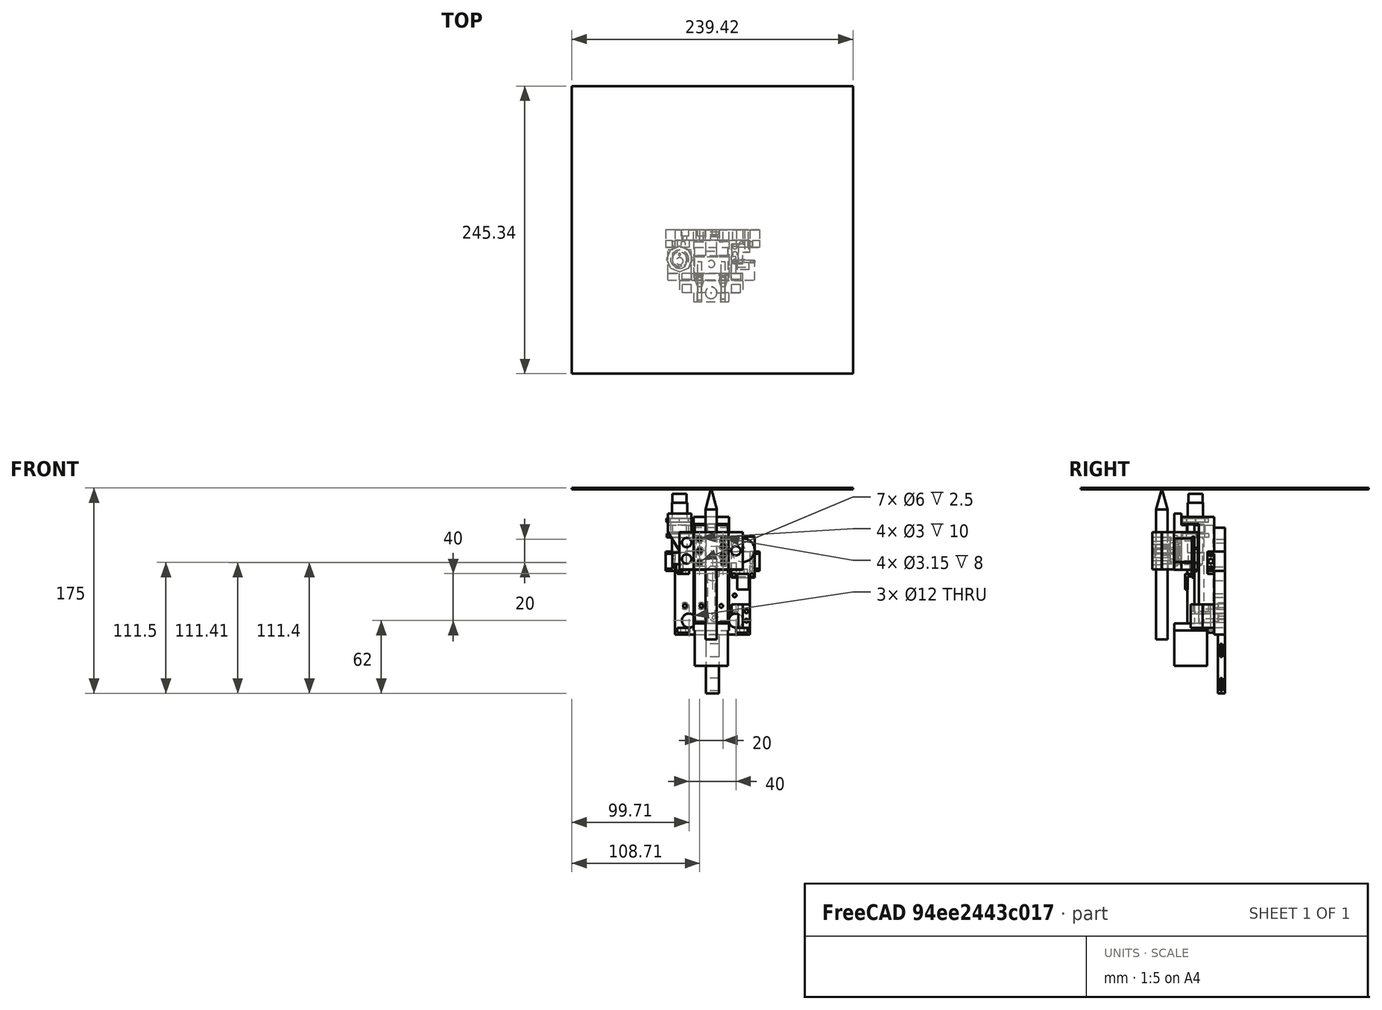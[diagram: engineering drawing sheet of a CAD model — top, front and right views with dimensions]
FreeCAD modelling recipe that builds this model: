
FCSTD DOCUMENT  (FreeCAD 1.0R39109 (Git))
Label: pen_plotter_head_v2a
License: All rights reserved
LicenseURL: https://en.wikipedia.org/wiki/All_rights_reserved
objects: Sketcher::SketchObject×76, PartDesign::Pad×47, PartDesign::Pocket×32, PartDesign::Body×13, PartDesign::Mirrored×5, PartDesign::LinearPattern×3, Mesh::Feature×2
note: 418 computed .brp shape members not serialized (recipe doc carries the construction recipe); baked Part::Feature solids carry a one-line shape summary decoded from their .brp

FEATURE [Mesh::Feature] Carriage_Plate_w_Threads
  Placement = pos=(32.05,21.1,32.2) rot=(0,0.707107,-0.707107;3.14159rad)
FEATURE [Mesh::Feature] _0x20_v_slot  label="20x20_v-slot"
  Placement = pos=(-48.6,20.5,0) rot=(0,0,-1;1.5708rad)
FEATURE [Sketcher::SketchObject] Sketch
  ArcFitTolerance = 1e-06
  AttachmentSupport = -> [XZ_Plane001]
  FullyConstrained = true
  MakeInternals = false
  MapMode = 5
  Placement = pos=(0,0,0) rot=(1,0,0;1.5708rad)
  sketch-geometry (5):
    g0: LineSegment StartX=-15 StartY=-48.5 StartZ=0 EndX=15 EndY=-48.5 EndZ=0
    g1: LineSegment StartX=15 StartY=-48.5 StartZ=0 EndX=15 EndY=48.5 EndZ=0
    g2: LineSegment StartX=15 StartY=48.5 StartZ=0 EndX=-15 EndY=48.5 EndZ=0
    g3: LineSegment StartX=-15 StartY=48.5 StartZ=0 EndX=-15 EndY=-48.5 EndZ=0
    g4: GeomPoint [constr] X=0 Y=0 Z=0
  constraints (12):
    c: Coincident(g0,g1)
    c: Coincident(g1,g2)
    c: Coincident(g2,g3)
    c: Coincident(g3,g0)
    c: Horizontal(g0)
    c: Horizontal(g2)
    c: Vertical(g1)
    c: Vertical(g3)
    c: Symmetric(g2,g0,g4)
    c: Distance(g1,g3) = 30
    c: Distance(g0,g2) = 97
    c: Coincident(g4,g-1)
FEATURE [PartDesign::Pad] Pad  label="Base"
  Direction = (0,-1,2e-16)
  Length = 13
  Length2 = 10
  Placement = pos=(0,0,0) rot=(1,0,0;1.5708rad)
  Profile = -> Sketch
  ReferenceAxis = -> Sketch [N_Axis]
  Refine = true
  Suppressed = false
  Type = 0
FEATURE [Sketcher::SketchObject] Sketch001
  ArcFitTolerance = 1e-06
  AttachmentSupport = -> [Pad]
  ExternalGeometry = -> [Pad]
  FullyConstrained = true
  MakeInternals = false
  MapMode = 5
  Placement = pos=(0,-13,0) rot=(1,0,0;1.5708rad)
  sketch-geometry (10):
    g0: LineSegment StartX=-15 StartY=-42.5 StartZ=0 EndX=-15 EndY=-48.5 EndZ=0
    g1: LineSegment StartX=-15 StartY=-48.5 StartZ=0 EndX=15 EndY=-48.5 EndZ=0
    g2: LineSegment StartX=15 StartY=-48.5 StartZ=0 EndX=15 EndY=-42.5 EndZ=0
    g3: LineSegment StartX=15 StartY=-42.5 StartZ=0 EndX=-15 EndY=-42.5 EndZ=0
    g4: GeomPoint [constr] X=0 Y=-45.5 Z=0
    g5: LineSegment StartX=-15 StartY=42.5 StartZ=0 EndX=15 EndY=42.5 EndZ=0
    g6: LineSegment StartX=15 StartY=42.5 StartZ=0 EndX=15 EndY=48.5 EndZ=0
    g7: LineSegment StartX=15 StartY=48.5 StartZ=0 EndX=-15 EndY=48.5 EndZ=0
    g8: LineSegment StartX=-15 StartY=48.5 StartZ=0 EndX=-15 EndY=42.5 EndZ=0
    g9: GeomPoint [constr] X=0 Y=45.5 Z=0
  constraints (24):
    c: Coincident(g0,g1)
    c: Coincident(g1,g2)
    c: Coincident(g2,g3)
    c: Coincident(g3,g0)
    c: Vertical(g0)
    c: Vertical(g2)
    c: Horizontal(g1)
    c: Horizontal(g3)
    c: Symmetric(g2,g0,g4)
    c: PointOnObject(g4,g-2)
    c: Coincident(g1,g-3)
    c: DistanceY(g1,g2) = 6
    c: Coincident(g5,g6)
    c: Coincident(g6,g7)
    c: Coincident(g7,g8)
    c: Coincident(g8,g5)
    c: Horizontal(g5)
    c: Horizontal(g7)
    c: Vertical(g6)
    c: Vertical(g8)
    c: Symmetric(g7,g5,g9)
    c: PointOnObject(g9,g-2)
    c: Coincident(g6,g-5)
    c: Equal(g6,g2)
FEATURE [PartDesign::Pad] Pad001  label="Flanges"
  BaseFeature = -> Pad
  Direction = (0,-1,2e-16)
  Length = 15
  Length2 = 10
  Placement = pos=(0,0,0) rot=(1,0,0;1.5708rad)
  Profile = -> Sketch001
  ReferenceAxis = -> Sketch001 [N_Axis]
  Refine = true
  Suppressed = false
  Type = 0
FEATURE [PartDesign::Pad] Pad002  label="FlangeExtension"
  BaseFeature = -> Pad001
  Direction = (0,-1,0)
  Length = 6
  Length2 = 10
  Placement = pos=(0,0,0) rot=(1,0,0;1.5708rad)
  Profile = -> Pad001 [Face5]
  Refine = true
  Suppressed = false
  Type = 0
FEATURE [Sketcher::SketchObject] Sketch002
  ArcFitTolerance = 1e-06
  AttachmentSupport = -> [Pad002]
  ExternalGeometry = -> [Pad002]
  FullyConstrained = true
  MakeInternals = false
  MapMode = 5
  Placement = pos=(0,2.09e-14,48.5) rot=(0,0,1;3.14159rad)
  sketch-geometry (5):
    g0: LineSegment StartX=-14 StartY=6 StartZ=0 EndX=14 EndY=6 EndZ=0
    g1: LineSegment StartX=14 StartY=6 StartZ=0 EndX=14 EndY=34 EndZ=0
    g2: LineSegment StartX=14 StartY=34 StartZ=0 EndX=-14 EndY=34 EndZ=0
    g3: LineSegment StartX=-14 StartY=34 StartZ=0 EndX=-14 EndY=6 EndZ=0
    g4: GeomPoint [constr] X=0 Y=20 Z=0
  constraints (13):
    c: Coincident(g0,g1)
    c: Coincident(g1,g2)
    c: Coincident(g2,g3)
    c: Coincident(g3,g0)
    c: Horizontal(g0)
    c: Horizontal(g2)
    c: Vertical(g1)
    c: Vertical(g3)
    c: Symmetric(g2,g0,g4)
    c: Distance(g1,g3) = 28
    c: PointOnObject(g2,g-3)
    c: PointOnObject(g4,g-2)
    c: Equal(g1,g2)
FEATURE [PartDesign::Pad] Pad003  label="Stepper"
  BaseFeature = -> Pad002
  Direction = (0,0,1)
  Length = 30
  Length2 = 10
  Placement = pos=(0,0,0) rot=(1,0,0;1.5708rad)
  Profile = -> Sketch002
  ReferenceAxis = -> Sketch002 [N_Axis]
  Refine = true
  Suppressed = false
  Type = 0
FEATURE [Sketcher::SketchObject] Sketch003
  ArcFitTolerance = 1e-06
  AttachmentSupport = -> [Pad003]
  FullyConstrained = false
  MakeInternals = false
  MapMode = 5
  Placement = pos=(0,-13,0) rot=(1,0,0;1.5708rad)
  sketch-geometry (5):
    g0: LineSegment StartX=-13 StartY=-32.4103 StartZ=0 EndX=13 EndY=-32.4103 EndZ=0
    g1: LineSegment StartX=13 StartY=-32.4103 StartZ=0 EndX=13 EndY=-6.41029 EndZ=0
    g2: LineSegment StartX=13 StartY=-6.41029 StartZ=0 EndX=-13 EndY=-6.41029 EndZ=0
    g3: LineSegment StartX=-13 StartY=-6.41029 StartZ=0 EndX=-13 EndY=-32.4103 EndZ=0
    g4: GeomPoint [constr] X=0 Y=-19.4103 Z=0
  constraints (12):
    c: Coincident(g0,g1)
    c: Coincident(g1,g2)
    c: Coincident(g2,g3)
    c: Coincident(g3,g0)
    c: Horizontal(g0)
    c: Horizontal(g2)
    c: Vertical(g1)
    c: Vertical(g3)
    c: Symmetric(g2,g0,g4)
    c: Distance(g1,g3) = 26
    c: Distance(g0,g2) = 26
    c: DistanceX(g-1,g4) = 0
FEATURE [PartDesign::Pad] Pad004  label="TableBase"
  BaseFeature = -> Pad003
  Direction = (0,-1,2e-16)
  Length = 1
  Length2 = 10
  Placement = pos=(0,0,0) rot=(1,0,0;1.5708rad)
  Profile = -> Sketch003
  ReferenceAxis = -> Sketch003 [N_Axis]
  Refine = true
  Suppressed = false
  Type = 0
FEATURE [Sketcher::SketchObject] Sketch004
  ArcFitTolerance = 1e-06
  AttachmentSupport = -> [Pad004]
  ExternalGeometry = -> [Pad004]
  FullyConstrained = true
  MakeInternals = false
  MapMode = 5
  Placement = pos=(0,-14,0) rot=(1,0,0;1.5708rad)
  sketch-geometry (8):
    g0: LineSegment StartX=-15 StartY=-35.4103 StartZ=0 EndX=15 EndY=-35.4103 EndZ=0
    g1: LineSegment StartX=15 StartY=-35.4103 StartZ=0 EndX=15 EndY=-3.41029 EndZ=0
    g2: LineSegment StartX=15 StartY=-3.41029 StartZ=0 EndX=-15 EndY=-3.41029 EndZ=0
    g3: LineSegment StartX=-15 StartY=-3.41029 StartZ=0 EndX=-15 EndY=-35.4103 EndZ=0
    g4: GeomPoint [constr] X=0 Y=-19.4103 Z=0
    g5: GeomPoint [constr] X=13 Y=-19.4103 Z=0
    g6: GeomPoint [constr] X=-3e-16 Y=-6.41029 Z=0
    g7: GeomPoint [constr] X=0 Y=-19.4103 Z=0
  constraints (16):
    c: Coincident(g0,g1)
    c: Coincident(g1,g2)
    c: Coincident(g2,g3)
    c: Coincident(g3,g0)
    c: Horizontal(g0)
    c: Horizontal(g2)
    c: Vertical(g1)
    c: Vertical(g3)
    c: Symmetric(g2,g0,g4)
    c: Distance(g1,g3) = 30
    c: Distance(g0,g2) = 32
    c: DistanceX(g-1,g4) = 0
    c: Symmetric(g-4,g-4,g5)
    c: Symmetric(g-3,g-3,g6)
    c: DistanceY(g5,g7) = 0
    c: Coincident(g4,g7)
FEATURE [PartDesign::Pad] Pad005  label="TableMount"
  BaseFeature = -> Pad004
  Direction = (0,-1,2e-16)
  Length = 14
  Length2 = 10
  Placement = pos=(0,0,0) rot=(1,0,0;1.5708rad)
  Profile = -> Sketch004
  ReferenceAxis = -> Sketch004 [N_Axis]
  Refine = true
  Suppressed = false
  Type = 0
FEATURE [Sketcher::SketchObject] Sketch005
  ArcFitTolerance = 1e-06
  AttachmentSupport = -> [Pad005]
  ExternalGeometry = -> [Pad005]
  FullyConstrained = true
  MakeInternals = false
  MapMode = 5
  Placement = pos=(0,-28,6.2e-15) rot=(1,0,0;1.5708rad)
  sketch-geometry (4):
    g0: Circle CenterX=-10 CenterY=-9.41029 CenterZ=0 NormalX=0 NormalY=0 NormalZ=1 AngleXU=0 Radius=1.5
    g1: Circle CenterX=10 CenterY=-9.41029 CenterZ=0 NormalX=0 NormalY=0 NormalZ=1 AngleXU=0 Radius=1.5
    g2: Circle CenterX=10 CenterY=-29.4103 CenterZ=0 NormalX=0 NormalY=0 NormalZ=1 AngleXU=0 Radius=1.5
    g3: Circle CenterX=-10 CenterY=-29.4103 CenterZ=0 NormalX=0 NormalY=0 NormalZ=1 AngleXU=0 Radius=1.5
  constraints (12):
    c: Diameter(g0) = 3
    c: Equal(g1,g0)
    c: Equal(g0,g3)
    c: Equal(g3,g2)
    c: DistanceY(g0,g-5) = 6
    c: DistanceX(g-5,g0) = 5
    c: DistanceY(g1,g0) = 0
    c: DistanceX(g3,g0) = 0
    c: DistanceY(g3,g2) = 0
    c: DistanceX(g2,g1) = 0
    c: DistanceY(g3,g0) = 20
    c: DistanceX(g0,g1) = 20
FEATURE [PartDesign::Pocket] Pocket  label="TableMountingHoles"
  BaseFeature = -> Pad005
  Direction = (0,1,-2e-16)
  Length = 10
  Length2 = 5
  Placement = pos=(0,0,0) rot=(1,0,0;1.5708rad)
  Profile = -> Sketch005
  ReferenceAxis = -> Sketch005 [N_Axis]
  Refine = true
  Suppressed = false
  Type = 0
FEATURE [Sketcher::SketchObject] Sketch006
  ArcFitTolerance = 1e-06
  AttachmentSupport = -> [Pocket]
  ExternalGeometry = -> [Pocket]
  FullyConstrained = true
  MakeInternals = false
  MapMode = 5
  Placement = pos=(0,2.55e-14,42.5) rot=(1,0,0;3.14159rad)
  sketch-geometry (1):
    g0: Circle CenterX=0 CenterY=20 CenterZ=0 NormalX=0 NormalY=0 NormalZ=1 AngleXU=0 Radius=3
  constraints (3):
    c: PointOnObject(g0,g-2)
    c: DistanceY(g0,g-3) = 14
    c: Diameter(g0) = 6
FEATURE [PartDesign::Pad] Pad006  label="BallScrew"
  BaseFeature = -> Pocket
  Direction = (0,0,-1)
  Length = 85
  Length2 = 10
  Placement = pos=(0,0,0) rot=(1,0,0;1.5708rad)
  Profile = -> Sketch006
  ReferenceAxis = -> Sketch006 [N_Axis]
  Refine = true
  Suppressed = false
  Type = 0
FEATURE [Sketcher::SketchObject] Sketch007
  ArcFitTolerance = 1e-06
  AttachmentSupport = -> [Pad006]
  FullyConstrained = true
  MakeInternals = false
  MapMode = 5
  Placement = pos=(0,-13,0) rot=(1,0,0;1.5708rad)
  sketch-geometry (5):
    g0: LineSegment StartX=-4.5 StartY=-42.5 StartZ=0 EndX=4.5 EndY=-42.5 EndZ=0
    g1: LineSegment StartX=4.5 StartY=-42.5 StartZ=0 EndX=4.5 EndY=42.5 EndZ=0
    g2: LineSegment StartX=4.5 StartY=42.5 StartZ=0 EndX=-4.5 EndY=42.5 EndZ=0
    g3: LineSegment StartX=-4.5 StartY=42.5 StartZ=0 EndX=-4.5 EndY=-42.5 EndZ=0
    g4: GeomPoint [constr] X=0 Y=0 Z=0
  constraints (12):
    c: Coincident(g0,g1)
    c: Coincident(g1,g2)
    c: Coincident(g2,g3)
    c: Coincident(g3,g0)
    c: Horizontal(g0)
    c: Horizontal(g2)
    c: Vertical(g1)
    c: Vertical(g3)
    c: Symmetric(g2,g0,g4)
    c: Distance(g1,g3) = 9
    c: Distance(g0,g2) = 85
    c: Coincident(g4,g-1)
FEATURE [Sketcher::SketchObject] Sketch009
  ArcFitTolerance = 1e-06
  AttachmentSupport = -> [XZ_Plane002]
  FullyConstrained = true
  MakeInternals = false
  MapMode = 5
  Placement = pos=(0,0,0) rot=(1,0,0;1.5708rad)
  sketch-geometry (7):
    g0: LineSegment StartX=-10 StartY=-17.5 StartZ=0 EndX=10 EndY=-17.5 EndZ=0
    g1: LineSegment StartX=10 StartY=-17.5 StartZ=0 EndX=10 EndY=17.5 EndZ=0
    g2: LineSegment StartX=10 StartY=17.5 StartZ=0 EndX=-10 EndY=17.5 EndZ=0
    g3: LineSegment StartX=-10 StartY=17.5 StartZ=0 EndX=-10 EndY=-17.5 EndZ=0
    g4: GeomPoint [constr] X=0 Y=0 Z=0
    g5: Circle CenterX=7.7 CenterY=15.2 CenterZ=0 NormalX=0 NormalY=0 NormalZ=1 AngleXU=0 Radius=1.5
    g6: Circle CenterX=-7.7 CenterY=15.2 CenterZ=0 NormalX=0 NormalY=0 NormalZ=1 AngleXU=0 Radius=1.5
  constraints (17):
    c: Coincident(g0,g1)
    c: Coincident(g1,g2)
    c: Coincident(g2,g3)
    c: Coincident(g3,g0)
    c: Horizontal(g0)
    c: Horizontal(g2)
    c: Vertical(g1)
    c: Vertical(g3)
    c: Symmetric(g2,g0,g4)
    c: Distance(g1,g3) = 20
    c: Distance(g0,g2) = 35
    c: Coincident(g4,g-1)
    c: Diameter(g5) = 3
    c: Equal(g5,g6)
    c: DistanceX(g5,g1) = 2.3
    c: DistanceY(g5,g1) = 2.3
    c: Symmetric(g6,g5,g-2)
FEATURE [PartDesign::Pad] Pad007  label="Base002"
  Direction = (0,-1,2e-16)
  Length = 2
  Length2 = 10
  Placement = pos=(0,0,0) rot=(1,0,0;1.5708rad)
  Profile = -> Sketch009
  ReferenceAxis = -> Sketch009 [N_Axis]
  Refine = true
  Suppressed = false
  Type = 0
FEATURE [Sketcher::SketchObject] Sketch010
  ArcFitTolerance = 1e-06
  AttachmentSupport = -> [Pad007]
  FullyConstrained = true
  MakeInternals = false
  MapMode = 5
  Placement = pos=(0,-2,0) rot=(1,0,0;1.5708rad)
  sketch-geometry (1):
    g0: Circle CenterX=0 CenterY=-6 CenterZ=0 NormalX=0 NormalY=0 NormalZ=1 AngleXU=0 Radius=10
  constraints (3):
    c: Diameter(g0) = 20
    c: PointOnObject(g0,g-2)
    c: DistanceY(g-3,g0) = 14
FEATURE [PartDesign::Pad] Pad008
  BaseFeature = -> Pad007
  Direction = (0,-1,2e-16)
  Length = 15
  Length2 = 10
  Placement = pos=(0,0,0) rot=(1,0,0;1.5708rad)
  Profile = -> Sketch010
  ReferenceAxis = -> Sketch010 [N_Axis]
  Refine = true
  Suppressed = false
  Type = 0
FEATURE [Sketcher::SketchObject] Sketch011
  ArcFitTolerance = 1e-06
  AttachmentSupport = -> [Pad008]
  ExternalGeometry = -> [Pad008]
  FullyConstrained = true
  MakeInternals = false
  MapMode = 5
  Placement = pos=(0,4e-16,0) rot=(-1,0,0;1.5708rad)
  sketch-geometry (1):
    g0: Circle CenterX=0 CenterY=7.5 CenterZ=0 NormalX=0 NormalY=0 NormalZ=1 AngleXU=0 Radius=1.5
  constraints (3):
    c: Diameter(g0) = 3
    c: PointOnObject(g0,g-2)
    c: DistanceY(g0,g-3) = 10
FEATURE [PartDesign::Pad] Pad009
  BaseFeature = -> Pad008
  Direction = (0,1,2e-16)
  Length = 1
  Length2 = 10
  Placement = pos=(0,0,0) rot=(1,0,0;1.5708rad)
  Profile = -> Sketch011
  ReferenceAxis = -> Sketch011 [N_Axis]
  Refine = true
  Suppressed = false
  Type = 0
FEATURE [Sketcher::SketchObject] Sketch012
  ArcFitTolerance = 1e-06
  AttachmentSupport = -> [Pad009]
  ExternalGeometry = -> [Pad009]
  FullyConstrained = true
  MakeInternals = false
  MapMode = 5
  Placement = pos=(0,-2,0) rot=(1,0,0;1.5708rad)
  sketch-geometry (5):
    g0: LineSegment StartX=-5 StartY=14.2 StartZ=0 EndX=5 EndY=14.2 EndZ=0
    g1: LineSegment StartX=5 StartY=14.2 StartZ=0 EndX=5 EndY=16.5 EndZ=0
    g2: LineSegment StartX=5 StartY=16.5 StartZ=0 EndX=-5 EndY=16.5 EndZ=0
    g3: LineSegment StartX=-5 StartY=16.5 StartZ=0 EndX=-5 EndY=14.2 EndZ=0
    g4: GeomPoint [constr] X=0 Y=15.35 Z=0
  constraints (13):
    c: Coincident(g0,g1)
    c: Coincident(g1,g2)
    c: Coincident(g2,g3)
    c: Coincident(g3,g0)
    c: Horizontal(g0)
    c: Horizontal(g2)
    c: Vertical(g1)
    c: Vertical(g3)
    c: Symmetric(g2,g0,g4)
    c: Distance(g1,g3) = 10
    c: Distance(g0,g2) = 2.3
    c: PointOnObject(g4,g-2)
    c: DistanceY(g4,g-3) = 2.15
FEATURE [PartDesign::Pad] Pad010
  BaseFeature = -> Pad009
  Direction = (0,-1,2e-16)
  Length = 6
  Length2 = 10
  Placement = pos=(0,0,0) rot=(1,0,0;1.5708rad)
  Profile = -> Sketch012
  ReferenceAxis = -> Sketch012 [N_Axis]
  Refine = true
  Suppressed = false
  Type = 0
FEATURE [Sketcher::SketchObject] Sketch013
  ArcFitTolerance = 1e-06
  AttachmentSupport = -> [Pad010]
  ExternalGeometry = -> [Pad010]
  FullyConstrained = true
  MakeInternals = false
  MapMode = 5
  Placement = pos=(0,7.3e-15,16.5) rot=(0,0,1;3.14159rad)
  sketch-geometry (5):
    g0: LineSegment StartX=5 StartY=5.7 StartZ=0 EndX=5 EndY=8 EndZ=0
    g1: LineSegment StartX=5 StartY=8 StartZ=0 EndX=-5 EndY=8 EndZ=0
    g2: LineSegment StartX=-5 StartY=8 StartZ=0 EndX=-5 EndY=5.7 EndZ=0
    g3: LineSegment StartX=-5 StartY=5.7 StartZ=0 EndX=5 EndY=5.7 EndZ=0
    g4: GeomPoint [constr] X=0 Y=6.85 Z=0
  constraints (12):
    c: Coincident(g0,g1)
    c: Coincident(g1,g2)
    c: Coincident(g2,g3)
    c: Coincident(g3,g0)
    c: Vertical(g0)
    c: Vertical(g2)
    c: Horizontal(g1)
    c: Horizontal(g3)
    c: Symmetric(g2,g0,g4)
    c: PointOnObject(g4,g-2)
    c: DistanceY(g0,g0) = 2.3
    c: Coincident(g0,g-3)
FEATURE [PartDesign::Pad] Pad011
  BaseFeature = -> Pad010
  Direction = (0,0,1)
  Length = 11
  Length2 = 10
  Placement = pos=(0,0,0) rot=(1,0,0;1.5708rad)
  Profile = -> Sketch013
  ReferenceAxis = -> Sketch013 [N_Axis]
  Refine = true
  Suppressed = false
  Type = 0
FEATURE [PartDesign::Body] Body002  label="ElectroMagnetKeyStudio25N5V"
  AllowCompound = false
  Group = -> [Sketch009,Pad007,Sketch010,Pad008,Sketch011,Pad009,Sketch012,Pad010,Sketch013,Pad011]
  Origin = -> Origin002
  Placement = pos=(26,-26,34) rot=(0,1,0;3.14159rad)
  Tip = -> Pad011
FEATURE [Sketcher::SketchObject] Sketch014
  ArcFitTolerance = 1e-06
  AttachmentSupport = -> [XY_Plane003]
  FullyConstrained = true
  MakeInternals = false
  MapMode = 5
  sketch-geometry (1):
    g0: Circle CenterX=0 CenterY=0 CenterZ=0 NormalX=0 NormalY=0 NormalZ=1 AngleXU=0 Radius=6
  constraints (2):
    c: Diameter(g0) = 12
    c: Coincident(g0,g-1)
FEATURE [PartDesign::Pad] Pad012  label="SensorHead"
  Direction = (0,0,1)
  Length = 7.5
  Length2 = 10
  Profile = -> Sketch014
  ReferenceAxis = -> Sketch014 [N_Axis]
  Refine = true
  Suppressed = false
  Type = 0
FEATURE [Sketcher::SketchObject] Sketch015
  ArcFitTolerance = 1e-06
  AttachmentSupport = -> [Pad012]
  FullyConstrained = true
  MakeInternals = false
  MapMode = 5
  Placement = pos=(0,0,7.5) rot=(0,0,1;0rad)
  sketch-geometry (1):
    g0: Circle CenterX=0 CenterY=0 CenterZ=0 NormalX=0 NormalY=0 NormalZ=1 AngleXU=0 Radius=6.5
  constraints (2):
    c: Diameter(g0) = 13
    c: Coincident(g0,g-1)
FEATURE [PartDesign::Pad] Pad013  label="SensorThread"
  BaseFeature = -> Pad012
  Direction = (0,0,1)
  Length = 42.5
  Length2 = 10
  Profile = -> Sketch015
  ReferenceAxis = -> Sketch015 [N_Axis]
  Refine = true
  Suppressed = false
  Type = 0
FEATURE [Sketcher::SketchObject] Sketch016
  ArcFitTolerance = 1e-06
  AttachmentSupport = -> [Pad013]
  FullyConstrained = true
  MakeInternals = false
  MapMode = 5
  Placement = pos=(0,0,50) rot=(0,0,1;0rad)
  sketch-geometry (1):
    g0: Circle CenterX=0 CenterY=0 CenterZ=0 NormalX=0 NormalY=0 NormalZ=1 AngleXU=0 Radius=6
  constraints (2):
    c: Diameter(g0) = 12
    c: Coincident(g0,g-1)
FEATURE [PartDesign::Pad] Pad014  label="SensorBody"
  BaseFeature = -> Pad013
  Direction = (0,0,1)
  Length = 10
  Length2 = 10
  Profile = -> Sketch016
  ReferenceAxis = -> Sketch016 [N_Axis]
  Refine = true
  Suppressed = false
  Type = 0
FEATURE [Sketcher::SketchObject] Sketch017
  ArcFitTolerance = 1e-06
  AttachmentSupport = -> [Pad014]
  FullyConstrained = false
  MakeInternals = false
  MapMode = 5
  Placement = pos=(0,0,60) rot=(0,0,1;0rad)
  sketch-geometry (1):
    g0: Circle CenterX=0 CenterY=-1.61854 CenterZ=0 NormalX=0 NormalY=0 NormalZ=1 AngleXU=0 Radius=3
  constraints (2):
    c: Diameter(g0) = 6
    c: PointOnObject(g0,g-2)
FEATURE [PartDesign::Pad] Pad015  label="SensorCable"
  BaseFeature = -> Pad014
  Direction = (0,0,1)
  Length = 6
  Length2 = 10
  Profile = -> Sketch017
  ReferenceAxis = -> Sketch017 [N_Axis]
  Refine = true
  Suppressed = false
  Type = 0
FEATURE [Sketcher::SketchObject] Sketch018
  ArcFitTolerance = 1e-06
  AttachmentSupport = -> [Pad015]
  FullyConstrained = false
  MakeInternals = false
  MapMode = 5
  Placement = pos=(0,0,60) rot=(0,0,1;0rad)
  sketch-geometry (1):
    g0: Circle CenterX=0 CenterY=4.04203 CenterZ=0 NormalX=0 NormalY=0 NormalZ=1 AngleXU=0 Radius=1
FEATURE [PartDesign::Pad] Pad016  label="SensorLED"
  BaseFeature = -> Pad015
  Direction = (0,0,1)
  Length = 1
  Length2 = 10
  Profile = -> Sketch018
  ReferenceAxis = -> Sketch018 [N_Axis]
  Refine = true
  Suppressed = false
  Type = 0
FEATURE [Sketcher::SketchObject] Sketch019
  ArcFitTolerance = 1e-06
  AttachmentOffset = pos=(0,0,-24) rot=(0,0,1;0rad)
  AttachmentSupport = -> [Pad016]
  FullyConstrained = false
  MakeInternals = false
  MapMode = 5
  Placement = pos=(0,0,24) rot=(1,0,0;3.14159rad)
  sketch-geometry (9):
    g0: LineSegment StartX=0 StartY=10.7223 StartZ=0 EndX=-7.73863 EndY=7.4066 EndZ=0
    g1: LineSegment StartX=-7.73863 StartY=7.4066 StartZ=0 EndX=-10.8661 EndY=-0.409983 EndZ=0
    g2: LineSegment StartX=-10.8661 StartY=-0.409983 StartZ=0 EndX=-7.55045 EndY=-8.14861 EndZ=0
    g3: LineSegment StartX=-7.55045 StartY=-8.14861 StartZ=0 EndX=0.266132 EndY=-11.2761 EndZ=0
    g4: LineSegment StartX=0.266132 StartY=-11.2761 StartZ=0 EndX=8.00476 EndY=-7.96043 EndZ=0
    g5: LineSegment StartX=8.00476 StartY=-7.96043 StartZ=0 EndX=11.1323 EndY=-0.143851 EndZ=0
    g6: LineSegment StartX=11.1323 StartY=-0.143851 StartZ=0 EndX=7.81658 EndY=7.59478 EndZ=0
    g7: LineSegment StartX=7.81658 StartY=7.59478 StartZ=0 EndX=0 EndY=10.7223 EndZ=0
    g8: Circle [constr] CenterX=0.133066 CenterY=-0.276917 CenterZ=0 NormalX=0 NormalY=0 NormalZ=1 AngleXU=0 Radius=11
  constraints (19):
    c: Coincident(g0,g1)
    c: Coincident(g1,g2)
    c: Coincident(g2,g3)
    c: Coincident(g3,g4)
    c: Coincident(g4,g5)
    c: Coincident(g5,g6)
    c: Coincident(g6,g7)
    c: Coincident(g7,g0)
    c: Equal(g0, g1-g7) x7
    c: PointOnObject(g0,g8)
    c: PointOnObject(g1,g8)
    c: PointOnObject(g2,g8)
    c: PointOnObject(g3,g8)
    c: PointOnObject(g4,g8)
    c: PointOnObject(g5,g8)
    c: PointOnObject(g6,g8)
    c: PointOnObject(g7,g8)
    c: Radius(g8) = 11
    c: PointOnObject(g7,g-2)
FEATURE [PartDesign::Pad] Pad017  label="SensorNut"
  BaseFeature = -> Pad016
  Direction = (0,0,-1)
  Length = 3
  Length2 = 10
  Profile = -> Sketch019
  ReferenceAxis = -> Sketch019 [N_Axis]
  Refine = true
  Suppressed = false
  Type = 0
FEATURE [Sketcher::SketchObject] Sketch020
  ArcFitTolerance = 1e-06
  AttachmentSupport = -> [Pad017]
  FullyConstrained = false
  MakeInternals = false
  MapMode = 5
  Placement = pos=(0,0,24) rot=(0,0,1;0rad)
  sketch-geometry (1):
    g0: Circle CenterX=0 CenterY=0 CenterZ=0 NormalX=0 NormalY=0 NormalZ=1 AngleXU=0 Radius=7.74183
  constraints (1):
    c: Coincident(g0,g-1)
FEATURE [PartDesign::Pad] Pad018  label="SensorSpacer"
  BaseFeature = -> Pad017
  Direction = (0,0,1)
  Length = 10
  Length2 = 10
  Profile = -> Sketch020
  ReferenceAxis = -> Sketch020 [N_Axis]
  Refine = true
  Suppressed = false
  Type = 0
FEATURE [Sketcher::SketchObject] Sketch021
  ArcFitTolerance = 1e-06
  AttachmentSupport = -> [Pad018]
  FullyConstrained = true
  MakeInternals = false
  MapMode = 5
  Placement = pos=(0,0,34) rot=(0,0,1;0rad)
  sketch-geometry (9):
    g0: LineSegment StartX=0 StartY=11 StartZ=0 EndX=-7.77817 EndY=7.77817 EndZ=0
    g1: LineSegment StartX=-7.77817 StartY=7.77817 StartZ=0 EndX=-11 EndY=-1.61604e-11 EndZ=0
    g2: LineSegment StartX=-11 StartY=-1.61604e-11 StartZ=0 EndX=-7.77817 EndY=-7.77817 EndZ=0
    g3: LineSegment StartX=-7.77817 StartY=-7.77817 StartZ=0 EndX=3.23208e-11 EndY=-11 EndZ=0
    g4: LineSegment StartX=3.23208e-11 StartY=-11 StartZ=0 EndX=7.77817 EndY=-7.77817 EndZ=0
    g5: LineSegment StartX=7.77817 StartY=-7.77817 StartZ=0 EndX=11 EndY=4.84821e-11 EndZ=0
    g6: LineSegment StartX=11 StartY=4.84821e-11 StartZ=0 EndX=7.77817 EndY=7.77817 EndZ=0
    g7: LineSegment StartX=7.77817 StartY=7.77817 StartZ=0 EndX=0 EndY=11 EndZ=0
    g8: Circle [constr] CenterX=0 CenterY=0 CenterZ=0 NormalX=0 NormalY=0 NormalZ=1 AngleXU=0 Radius=11
  constraints (20):
    c: Coincident(g0,g1)
    c: Coincident(g1,g2)
    c: Coincident(g2,g3)
    c: Coincident(g3,g4)
    c: Coincident(g4,g5)
    c: Coincident(g5,g6)
    c: Coincident(g6,g7)
    c: Coincident(g7,g0)
    c: Equal(g0, g1-g7) x7
    c: PointOnObject(g0,g8)
    c: PointOnObject(g1,g8)
    c: PointOnObject(g2,g8)
    c: PointOnObject(g3,g8)
    c: PointOnObject(g4,g8)
    c: PointOnObject(g5,g8)
    c: PointOnObject(g6,g8)
    c: PointOnObject(g7,g8)
    c: Radius(g8) = 11
    c: Coincident(g8,g-1)
    c: PointOnObject(g7,g-2)
FEATURE [PartDesign::Pad] Pad019  label="SensorNut2"
  BaseFeature = -> Pad018
  Direction = (0,0,1)
  Length = 3
  Length2 = 10
  Profile = -> Sketch021
  ReferenceAxis = -> Sketch021 [N_Axis]
  Refine = true
  Suppressed = false
  Type = 0
FEATURE [PartDesign::Body] Body003  label="InductiveProximitySensorM12"
  AllowCompound = false
  Group = -> [Sketch014,Pad012,Sketch015,Pad013,Sketch016,Pad014,Sketch017,Pad015,Sketch018,Pad016,Sketch019,Pad017,Sketch020,Pad018,Sketch021,Pad019]
  Origin = -> Origin003
  Placement = pos=(-28,-25,88) rot=(0,1,0;3.14159rad)
  Tip = -> Pad019
FEATURE [Sketcher::SketchObject] Sketch022
  ArcFitTolerance = 1e-06
  AttachmentSupport = -> [XZ_Plane]
  FullyConstrained = true
  MakeInternals = false
  MapMode = 5
  Placement = pos=(0,0,0) rot=(1,0,0;1.5708rad)
  sketch-geometry (5):
    g0: LineSegment StartX=-32 StartY=-32 StartZ=0 EndX=32 EndY=-32 EndZ=0
    g1: LineSegment StartX=32 StartY=-32 StartZ=0 EndX=32 EndY=32 EndZ=0
    g2: LineSegment StartX=32 StartY=32 StartZ=0 EndX=-32 EndY=32 EndZ=0
    g3: LineSegment StartX=-32 StartY=32 StartZ=0 EndX=-32 EndY=-32 EndZ=0
    g4: GeomPoint [constr] X=0 Y=0 Z=0
  constraints (12):
    c: Coincident(g0,g1)
    c: Coincident(g1,g2)
    c: Coincident(g2,g3)
    c: Coincident(g3,g0)
    c: Horizontal(g0)
    c: Horizontal(g2)
    c: Vertical(g1)
    c: Vertical(g3)
    c: Symmetric(g2,g0,g4)
    c: Distance(g1,g3) = 64
    c: Distance(g0,g2) = 64
    c: Coincident(g4,g-1)
FEATURE [PartDesign::Pad] Pad020  label="BackingPlate"
  Direction = (0,-1,2e-16)
  Length = 9
  Length2 = 10
  Placement = pos=(0,0,0) rot=(1,0,0;1.5708rad)
  Profile = -> Sketch022
  ReferenceAxis = -> Sketch022 [N_Axis]
  Refine = true
  Suppressed = false
  Type = 0
FEATURE [Sketcher::SketchObject] Sketch023
  ArcFitTolerance = 1e-06
  AttachmentSupport = -> [Pad020]
  ExternalGeometry = -> [Pad020]
  FullyConstrained = true
  MakeInternals = false
  MapMode = 5
  Placement = pos=(0,0,0) rot=(-1,0,0;1.5708rad)
  sketch-geometry (2):
    g0: Circle CenterX=-9.5 CenterY=7.5 CenterZ=0 NormalX=0 NormalY=0 NormalZ=1 AngleXU=0 Radius=1.55
    g1: Circle CenterX=-23.5 CenterY=7.5 CenterZ=0 NormalX=0 NormalY=0 NormalZ=1 AngleXU=0 Radius=1.55
  constraints (6):
    c: Diameter(g0) = 3.1
    c: Equal(g1,g0)
    c: DistanceY(g1,g0) = 0
    c: DistanceY(g1,g-3) = 24.5
    c: DistanceX(g-4,g1) = 8.5
    c: DistanceX(g1,g0) = 14
FEATURE [PartDesign::Pocket] Pocket003  label="CaptiveNutScrewHole"
  BaseFeature = -> Pad020
  Direction = (0,-1,-2e-16)
  Length = 9
  Length2 = 5
  Placement = pos=(0,0,0) rot=(1,0,0;1.5708rad)
  Profile = -> Sketch023
  ReferenceAxis = -> Sketch023 [N_Axis]
  Refine = true
  Suppressed = false
  Type = 0
FEATURE [Sketcher::SketchObject] Sketch024
  ArcFitTolerance = 1e-06
  AttachmentSupport = -> [Pocket003]
  ExternalGeometry = -> [Pocket003]
  FullyConstrained = true
  MakeInternals = false
  MapMode = 5
  Placement = pos=(0,0,0) rot=(-1,0,0;1.5708rad)
  sketch-geometry (2):
    g0: Circle CenterX=1.4 CenterY=17.5 CenterZ=0 NormalX=0 NormalY=0 NormalZ=1 AngleXU=0 Radius=1.55
    g1: Circle CenterX=18.9 CenterY=-1.5 CenterZ=0 NormalX=0 NormalY=0 NormalZ=1 AngleXU=0 Radius=1.55
  constraints (6):
    c: Diameter(g0) = 3.1
    c: Diameter(g1) = 3.1
    c: DistanceY(g0,g-4) = 14.5
    c: DistanceY(g1,g0) = 19
    c: DistanceX(g1,g-4) = 13.1
    c: DistanceX(g0,g1) = 17.5
FEATURE [PartDesign::Pocket] Pocket004  label="ThreadedHoleScrewHole"
  BaseFeature = -> Pocket003
  Direction = (0,-1,-2e-16)
  Length = 9
  Length2 = 5
  Placement = pos=(0,0,0) rot=(1,0,0;1.5708rad)
  Profile = -> Sketch024
  ReferenceAxis = -> Sketch024 [N_Axis]
  Refine = true
  Suppressed = false
  Type = 0
FEATURE [Sketcher::SketchObject] Sketch025
  ArcFitTolerance = 1e-06
  AttachmentSupport = -> [Pocket004]
  ExternalGeometry = -> [Pocket004]
  FullyConstrained = true
  MakeInternals = false
  MapMode = 5
  Placement = pos=(0,0,0) rot=(-1,0,0;1.5708rad)
  sketch-geometry (2):
    g0: Circle CenterX=-23.5 CenterY=7.5 CenterZ=0 NormalX=0 NormalY=0 NormalZ=1 AngleXU=0 Radius=3
    g1: Circle CenterX=-9.5 CenterY=7.5 CenterZ=0 NormalX=0 NormalY=0 NormalZ=1 AngleXU=0 Radius=3
  constraints (4):
    c: Diameter(g0) = 6
    c: Coincident(g0,g-3)
    c: Diameter(g1) = 6
    c: Coincident(g1,g-4)
FEATURE [PartDesign::Pocket] Pocket005  label="CaptiveNutHole"
  BaseFeature = -> Pocket004
  Direction = (0,-1,-2e-16)
  Length = 5.5
  Length2 = 5
  Placement = pos=(0,0,0) rot=(1,0,0;1.5708rad)
  Profile = -> Sketch025
  ReferenceAxis = -> Sketch025 [N_Axis]
  Refine = true
  Suppressed = false
  Type = 0
FEATURE [Sketcher::SketchObject] Sketch026
  ArcFitTolerance = 1e-06
  AttachmentSupport = -> [Pocket005]
  ExternalGeometry = -> [Pocket005]
  FullyConstrained = true
  MakeInternals = false
  MapMode = 5
  Placement = pos=(0,0,0) rot=(-1,0,0;1.5708rad)
  sketch-geometry (3):
    g0: Circle CenterX=0 CenterY=-20 CenterZ=0 NormalX=0 NormalY=0 NormalZ=1 AngleXU=0 Radius=6
    g1: Circle CenterX=20 CenterY=20 CenterZ=0 NormalX=0 NormalY=0 NormalZ=1 AngleXU=0 Radius=6
    g2: Circle CenterX=-20 CenterY=20 CenterZ=0 NormalX=0 NormalY=0 NormalZ=1 AngleXU=0 Radius=6
  constraints (9):
    c: Diameter(g0) = 12
    c: PointOnObject(g0,g-2)
    c: Equal(g0,g1)
    c: DistanceX(g1,g-3) = 12
    c: DistanceX(g2,g1) = 40
    c: DistanceY(g1,g2) = 0
    c: DistanceY(g1,g-3) = 12
    c: DistanceY(g0,g-3) = 52
    c: Equal(g2,g1)
FEATURE [PartDesign::Pocket] Pocket006  label="WheelNutCutouts"
  BaseFeature = -> Pocket005
  Direction = (0,-1,-2e-16)
  Length = 9
  Length2 = 5
  Placement = pos=(0,0,0) rot=(1,0,0;1.5708rad)
  Profile = -> Sketch026
  ReferenceAxis = -> Sketch026 [N_Axis]
  Refine = true
  Suppressed = false
  Type = 0
FEATURE [Sketcher::SketchObject] Sketch027
  ArcFitTolerance = 1e-06
  AttachmentSupport = -> [XY_Plane004]
  FullyConstrained = false
  MakeInternals = false
  MapMode = 5
  sketch-geometry (5):
    g0: LineSegment StartX=119.707 StartY=-122.67 StartZ=0 EndX=119.707 EndY=122.67 EndZ=0
    g1: LineSegment StartX=119.707 StartY=122.67 StartZ=0 EndX=-119.707 EndY=122.67 EndZ=0
    g2: LineSegment StartX=-119.707 StartY=122.67 StartZ=0 EndX=-119.707 EndY=-122.67 EndZ=0
    g3: LineSegment StartX=-119.707 StartY=-122.67 StartZ=0 EndX=119.707 EndY=-122.67 EndZ=0
    g4: GeomPoint [constr] X=0 Y=0 Z=0
  constraints (10):
    c: Coincident(g0,g1)
    c: Coincident(g1,g2)
    c: Coincident(g2,g3)
    c: Coincident(g3,g0)
    c: Vertical(g0)
    c: Vertical(g2)
    c: Horizontal(g1)
    c: Horizontal(g3)
    c: Symmetric(g2,g0,g4)
    c: Coincident(g4,g-1)
FEATURE [PartDesign::Pad] Pad021
  Direction = (0,0,1)
  Length = 1
  Length2 = 10
  Profile = -> Sketch027
  ReferenceAxis = -> Sketch027 [N_Axis]
  Refine = true
  Suppressed = false
  Type = 0
FEATURE [PartDesign::Body] Body004  label="DrawingPlate"
  AllowCompound = false
  Group = -> [Sketch027,Pad021]
  Origin = -> Origin004
  Placement = pos=(0,0,92) rot=(0,0,1;0rad)
  Tip = -> Pad021
FEATURE [PartDesign::Pocket] Pocket001  label="Slide"
  BaseFeature = -> Pad006
  Direction = (0,1,-2e-16)
  Length = 4
  Length2 = 5
  Placement = pos=(0,0,0) rot=(1,0,0;1.5708rad)
  Profile = -> Sketch007
  ReferenceAxis = -> Sketch007 [N_Axis]
  Refine = true
  Suppressed = false
  Type = 0
FEATURE [Sketcher::SketchObject] Sketch008
  ArcFitTolerance = 1e-06
  AttachmentSupport = -> [Pocket001]
  ExternalGeometry = -> [Pocket001]
  FullyConstrained = true
  MakeInternals = false
  MapMode = 5
  Placement = pos=(0,0,0) rot=(-1,0,0;1.5708rad)
  sketch-geometry (4):
    g0: Circle CenterX=-8.5 CenterY=27.5 CenterZ=0 NormalX=0 NormalY=0 NormalZ=1 AngleXU=0 Radius=1.5
    g1: Circle CenterX=8.5 CenterY=27.5 CenterZ=0 NormalX=0 NormalY=0 NormalZ=1 AngleXU=0 Radius=1.5
    g2: Circle CenterX=8.5 CenterY=-27.5 CenterZ=0 NormalX=0 NormalY=0 NormalZ=1 AngleXU=0 Radius=1.5
    g3: Circle CenterX=-8.5 CenterY=-27.5 CenterZ=0 NormalX=0 NormalY=0 NormalZ=1 AngleXU=0 Radius=1.5
  constraints (10):
    c: Diameter(g0) = 3
    c: Equal(g3,g2)
    c: Equal(g2,g1)
    c: Equal(g1,g0)
    c: DistanceY(g0,g-3) = 21
    c: DistanceX(g0,g1) = 17
    c: Symmetric(g1,g0,g-2)
    c: DistanceX(g3,g2) = 17
    c: Symmetric(g3,g2,g-2)
    c: DistanceY(g-4,g3) = 21
FEATURE [PartDesign::Pocket] Pocket002  label="MountingHoles"
  BaseFeature = -> Pocket001
  Direction = (0,-1,-2e-16)
  Length = 14
  Length2 = 5
  Placement = pos=(0,0,0) rot=(1,0,0;1.5708rad)
  Profile = -> Sketch008
  ReferenceAxis = -> Sketch008 [N_Axis]
  Refine = true
  Suppressed = false
  Type = 0
FEATURE [Sketcher::SketchObject] Sketch028
  ArcFitTolerance = 1e-06
  AttachmentSupport = -> [Pocket002]
  ExternalGeometry = -> [Pocket002]
  FullyConstrained = true
  MakeInternals = false
  MapMode = 5
  Placement = pos=(0,-13,0) rot=(1,0,0;1.5708rad)
  sketch-geometry (5):
    g0: LineSegment StartX=-4.5 StartY=-41.5 StartZ=0 EndX=-4.5 EndY=41.5 EndZ=0
    g1: LineSegment StartX=-4.5 StartY=41.5 StartZ=0 EndX=-14 EndY=41.5 EndZ=0
    g2: LineSegment StartX=-14 StartY=41.5 StartZ=0 EndX=-14 EndY=-41.5 EndZ=0
    g3: LineSegment StartX=-14 StartY=-41.5 StartZ=0 EndX=-4.5 EndY=-41.5 EndZ=0
    g4: GeomPoint [constr] X=-9.25 Y=0 Z=0
  constraints (13):
    c: Coincident(g0,g1)
    c: Coincident(g1,g2)
    c: Coincident(g2,g3)
    c: Coincident(g3,g0)
    c: Vertical(g0)
    c: Vertical(g2)
    c: Horizontal(g1)
    c: Horizontal(g3)
    c: Symmetric(g2,g0,g4)
    c: PointOnObject(g4,g-1)
    c: DistanceY(g1,g-4) = 1
    c: DistanceX(g-4,g1) = 1
    c: DistanceX(g0,g-3) = 0
FEATURE [PartDesign::Pocket] Pocket007  label="SlideInsetLeft"
  BaseFeature = -> Pocket002
  Direction = (0,1,-2e-16)
  Length = 12
  Length2 = 5
  Placement = pos=(0,0,0) rot=(1,0,0;1.5708rad)
  Profile = -> Sketch028
  ReferenceAxis = -> Sketch028 [N_Axis]
  Refine = true
  Suppressed = false
  Type = 0
FEATURE [Sketcher::SketchObject] Sketch029
  ArcFitTolerance = 1e-06
  AttachmentSupport = -> [Pocket007]
  ExternalGeometry = -> [Pocket007]
  FullyConstrained = true
  MakeInternals = false
  MapMode = 5
  Placement = pos=(0,-13,0) rot=(1,0,0;1.5708rad)
  sketch-geometry (5):
    g0: LineSegment StartX=4.5 StartY=-41.5 StartZ=0 EndX=14 EndY=-41.5 EndZ=0
    g1: LineSegment StartX=14 StartY=-41.5 StartZ=0 EndX=14 EndY=41.5 EndZ=0
    g2: LineSegment StartX=14 StartY=41.5 StartZ=0 EndX=4.5 EndY=41.5 EndZ=0
    g3: LineSegment StartX=4.5 StartY=41.5 StartZ=0 EndX=4.5 EndY=-41.5 EndZ=0
    g4: GeomPoint [constr] X=9.25 Y=0 Z=0
  constraints (13):
    c: Coincident(g0,g1)
    c: Coincident(g1,g2)
    c: Coincident(g2,g3)
    c: Coincident(g3,g0)
    c: Horizontal(g0)
    c: Horizontal(g2)
    c: Vertical(g1)
    c: Vertical(g3)
    c: Symmetric(g2,g0,g4)
    c: PointOnObject(g4,g-1)
    c: DistanceY(g1,g-3) = 1
    c: DistanceX(g1,g-3) = 1
    c: DistanceX(g-4,g2) = 0
FEATURE [PartDesign::Pocket] Pocket008  label="SlideInsetRight"
  BaseFeature = -> Pocket007
  Direction = (0,1,-2e-16)
  Length = 12
  Length2 = 5
  Placement = pos=(0,0,0) rot=(1,0,0;1.5708rad)
  Profile = -> Sketch029
  ReferenceAxis = -> Sketch029 [N_Axis]
  Refine = true
  Suppressed = false
  Type = 0
FEATURE [PartDesign::Body] Body001  label="SlideTable50mm"
  AllowCompound = false
  Group = -> [Sketch,Pad,Sketch001,Pad001,Pad002,Sketch002,Pad003,Sketch003,Pad004,Sketch004,Pad005,Sketch005,Pocket,Sketch006,Pad006,Sketch007,Pocket001,Sketch008,Pocket002,Sketch028,Pocket007,Sketch029,Pocket008]
  Origin = -> Origin001
  Placement = pos=(-1,-9,20) rot=(0,1,0;3.14159rad)
  Tip = -> Pocket008
FEATURE [Sketcher::SketchObject] Sketch030
  ArcFitTolerance = 1e-06
  AttachmentSupport = -> [Pocket006]
  ExternalGeometry = -> [Pocket006]
  FullyConstrained = false
  MakeInternals = false
  MapMode = 5
  Placement = pos=(0,-9,0) rot=(1,0,0;1.5708rad)
  sketch-geometry (4):
    g0: Circle CenterX=7.5 CenterY=-7.5 CenterZ=0 NormalX=0 NormalY=0 NormalZ=1 AngleXU=0 Radius=1.55
    g1: LineSegment [constr] StartX=-9.5 StartY=-7.5 StartZ=0 EndX=7.5 EndY=-7.5 EndZ=0
    g2: GeomPoint [constr] X=-1 Y=-7.5 Z=0
    g3: LineSegment [constr] StartX=-1 StartY=-7.5 StartZ=0 EndX=-1 EndY=141.426 EndZ=0
  constraints (8):
    c: DistanceX(g-3,g0) = 17
    c: DistanceY(g-3,g0) = 0
    c: Diameter(g0) = 3.1
    c: Coincident(g1,g-3)
    c: Coincident(g1,g0)
    c: Symmetric(g1,g1,g2)
    c: Vertical(g3)
    c: Coincident(g3,g2)
FEATURE [PartDesign::Pocket] Pocket009  label="SlideTopMountSecondScrewThreaded"
  BaseFeature = -> Pocket006
  Direction = (0,1,-2e-16)
  Length = 9
  Length2 = 5
  Placement = pos=(0,0,0) rot=(1,0,0;1.5708rad)
  Profile = -> Sketch030
  ReferenceAxis = -> Sketch030 [N_Axis]
  Refine = true
  Suppressed = false
  Type = 0
FEATURE [Sketcher::SketchObject] Sketch031
  ArcFitTolerance = 1e-06
  AttachmentSupport = -> [Pocket009]
  ExternalGeometry = -> [Pocket009]
  FullyConstrained = false
  MakeInternals = false
  MapMode = 5
  Placement = pos=(0,-9,0) rot=(1,0,0;1.5708rad)
  sketch-geometry (7):
    g0: LineSegment [constr] StartX=-9.5 StartY=-7.5 StartZ=0 EndX=7.5 EndY=-7.5 EndZ=0
    g1: LineSegment [constr] StartX=-1 StartY=-7.5 StartZ=0 EndX=-1 EndY=92.4566 EndZ=0
    g2: LineSegment StartX=-16 StartY=32 StartZ=0 EndX=14 EndY=32 EndZ=0
    g3: LineSegment StartX=14 StartY=32 StartZ=0 EndX=14 EndY=59.2274 EndZ=0
    g4: LineSegment StartX=14 StartY=59.2274 StartZ=0 EndX=-16 EndY=59.2274 EndZ=0
    g5: LineSegment StartX=-16 StartY=59.2274 StartZ=0 EndX=-16 EndY=32 EndZ=0
    g6: GeomPoint [constr] X=-1 Y=45.6137 Z=0
  constraints (16):
    c: Coincident(g0,g-3)
    c: Coincident(g0,g-4)
    c: Coincident(g2,g3)
    c: Coincident(g3,g4)
    c: Coincident(g4,g5)
    c: Coincident(g5,g2)
    c: Horizontal(g2)
    c: Horizontal(g4)
    c: Vertical(g3)
    c: Vertical(g5)
    c: Symmetric(g4,g2,g6)
    c: Distance(g3,g5) = 30
    c: PointOnObject(g6,g1)
    c: DistanceY(g-5,g2) = 0
    c: Parallel(g5,g1)
    c: Symmetric(g0,g0,g1)
FEATURE [PartDesign::Pad] Pad022  label="SlideSupportExtension"
  BaseFeature = -> Pocket009
  Direction = (0,-1,2e-16)
  Length = 9
  Length2 = 10
  Placement = pos=(0,0,0) rot=(1,0,0;1.5708rad)
  Profile = -> Sketch031
  ReferenceAxis = -> Sketch031 [N_Axis]
  Refine = true
  Reversed = true
  Suppressed = false
  Type = 0
FEATURE [Sketcher::SketchObject] Sketch032
  ArcFitTolerance = 1e-06
  AttachmentSupport = -> [Pad022]
  ExternalGeometry = -> [Pad022]
  FullyConstrained = true
  MakeInternals = false
  MapMode = 5
  Placement = pos=(0,-9,2.9e-15) rot=(1,0,0;1.5708rad)
  sketch-geometry (4):
    g0: Circle CenterX=-9.5 CenterY=47.5 CenterZ=0 NormalX=0 NormalY=0 NormalZ=1 AngleXU=0 Radius=1.55
    g1: Circle CenterX=7.5 CenterY=47.5 CenterZ=0 NormalX=0 NormalY=0 NormalZ=1 AngleXU=0 Radius=1.55
    g2: GeomPoint [constr] X=-1 Y=59.2274 Z=0
    g3: LineSegment [constr] StartX=-1 StartY=59.2274 StartZ=0 EndX=-1 EndY=47.5 EndZ=0
  constraints (9):
    c: Diameter(g0) = 3.1
    c: Equal(g1,g0)
    c: DistanceX(g0,g1) = 17
    c: Symmetric(g-3,g-3,g2)
    c: Symmetric(g0,g1,g3)
    c: Parallel(g3,g-2)
    c: DistanceY(g1,g0) = 0
    c: DistanceY(g-4,g1) = 55
    c: Coincident(g3,g2)
FEATURE [PartDesign::Pocket] Pocket010  label="SlideSupportExtensionMountHolesThreaded"
  BaseFeature = -> Pad022
  Direction = (0,1,-2e-16)
  Length = 9
  Length2 = 5
  Placement = pos=(0,0,0) rot=(1,0,0;1.5708rad)
  Profile = -> Sketch032
  ReferenceAxis = -> Sketch032 [N_Axis]
  Refine = true
  Suppressed = false
  Type = 0
FEATURE [Sketcher::SketchObject] Sketch033
  ArcFitTolerance = 1e-06
  AttachmentSupport = -> [XZ_Plane005]
  FullyConstrained = true
  MakeInternals = false
  MapMode = 5
  Placement = pos=(0,0,0) rot=(1,0,0;1.5708rad)
  sketch-geometry (4):
    g0: LineSegment StartX=-15 StartY=-16 StartZ=0 EndX=15 EndY=-16 EndZ=0
    g1: LineSegment StartX=15 StartY=-16 StartZ=0 EndX=15 EndY=16 EndZ=0
    g2: LineSegment StartX=15 StartY=16 StartZ=0 EndX=-15 EndY=16 EndZ=0
    g3: LineSegment StartX=-15 StartY=16 StartZ=0 EndX=-15 EndY=-16 EndZ=0
  constraints (11):
    c: Coincident(g0,g1)
    c: Coincident(g1,g2)
    c: Coincident(g2,g3)
    c: Coincident(g3,g0)
    c: Horizontal(g0)
    c: Horizontal(g2)
    c: Vertical(g1)
    c: Vertical(g3)
    c: Distance(g1,g3) = 30
    c: Distance(g0,g2) = 32
    c: Symmetric(g1,g0,g-1)
FEATURE [PartDesign::Pad] Pad023  label="Base001"
  Direction = (0,-1,2e-16)
  Length = 6
  Length2 = 10
  Placement = pos=(0,0,0) rot=(1,0,0;1.5708rad)
  Profile = -> Sketch033
  ReferenceAxis = -> Sketch033 [N_Axis]
  Refine = true
  Suppressed = false
  Type = 0
FEATURE [Sketcher::SketchObject] Sketch034
  ArcFitTolerance = 1e-06
  AttachmentSupport = -> [Pad023]
  FullyConstrained = true
  MakeInternals = false
  MapMode = 5
  Placement = pos=(0,-6,0) rot=(1,0,0;1.5708rad)
  sketch-geometry (12):
    g0: LineSegment StartX=-15 StartY=16 StartZ=0 EndX=15 EndY=16 EndZ=0
    g1: LineSegment StartX=15 StartY=16 StartZ=0 EndX=27 EndY=16 EndZ=0
    g2: LineSegment StartX=15 StartY=-16 StartZ=0 EndX=-15 EndY=-16 EndZ=0
    g3: LineSegment StartX=-37 StartY=16 StartZ=0 EndX=-37 EndY=32 EndZ=0
    g4: LineSegment StartX=-37 StartY=32 StartZ=0 EndX=-17 EndY=32 EndZ=0
    g5: LineSegment StartX=-17 StartY=32 StartZ=0 EndX=-17 EndY=16 EndZ=0
    g6: LineSegment StartX=-17 StartY=16 StartZ=0 EndX=-15 EndY=16 EndZ=0
    g7: LineSegment StartX=27 StartY=16 StartZ=0 EndX=27 EndY=-16 EndZ=0
    g8: LineSegment StartX=27 StartY=-16 StartZ=0 EndX=15 EndY=-16 EndZ=0
    g9: LineSegment StartX=-37 StartY=16 StartZ=0 EndX=-27 EndY=0 EndZ=0
    g10: LineSegment StartX=-27 StartY=0 StartZ=0 EndX=-27 EndY=-16 EndZ=0
    g11: LineSegment StartX=-27 StartY=-16 StartZ=0 EndX=-15 EndY=-16 EndZ=0
  constraints (32):
    c: Coincident(g-3,g0)
    c: Coincident(g0,g-3)
    c: Coincident(g0,g1)
    c: Horizontal(g1)
    c: Coincident(g2,g-4)
    c: Vertical(g3)
    c: Coincident(g3,g4)
    c: Horizontal(g4)
    c: Coincident(g4,g5)
    c: Vertical(g5)
    c: Coincident(g5,g6)
    c: Coincident(g6,g0)
    c: DistanceY(g5,g0) = 0
    c: DistanceX(g6,g6) = 2
    c: DistanceY(g3,g5) = 0
    c: DistanceX(g4,g4) = 20
    c: DistanceY(g3,g3) = 16
    c: Coincident(g1,g7)
    c: Vertical(g7)
    c: Coincident(g7,g8)
    c: Coincident(g8,g2)
    c: Horizontal(g8)
    c: DistanceX(g8,g8) = 12
    c: Coincident(g2,g-4)
    c: Coincident(g3,g9)
    c: Coincident(g9,g10)
    c: Vertical(g10)
    c: Coincident(g10,g11)
    c: Coincident(g11,g2)
    c: Horizontal(g11)
    c: Equal(g11,g8)
    c: PointOnObject(g9,g-1)
FEATURE [PartDesign::Pad] Pad024  label="Extensions"
  BaseFeature = -> Pad023
  Direction = (0,-1,2e-16)
  Length = 6
  Length2 = 10
  Placement = pos=(0,0,0) rot=(1,0,0;1.5708rad)
  Profile = -> Sketch034
  ReferenceAxis = -> Sketch034 [N_Axis]
  Refine = true
  Reversed = true
  Suppressed = false
  Type = 0
FEATURE [Sketcher::SketchObject] Sketch035
  ArcFitTolerance = 1e-06
  AttachmentSupport = -> [Pad024]
  FullyConstrained = true
  MakeInternals = false
  MapMode = 5
  Placement = pos=(0,-6,2.3e-15) rot=(1,0,0;1.5708rad)
  sketch-geometry (5):
    g0: GeomPoint [constr] X=0 Y=0 Z=0
    g1: Circle CenterX=-10 CenterY=10 CenterZ=0 NormalX=0 NormalY=0 NormalZ=1 AngleXU=0 Radius=1.575
    g2: Circle CenterX=10 CenterY=10 CenterZ=0 NormalX=0 NormalY=0 NormalZ=1 AngleXU=0 Radius=1.575
    g3: Circle CenterX=10 CenterY=-10 CenterZ=0 NormalX=0 NormalY=0 NormalZ=1 AngleXU=0 Radius=1.575
    g4: Circle CenterX=-10 CenterY=-10 CenterZ=0 NormalX=0 NormalY=0 NormalZ=1 AngleXU=0 Radius=1.575
  constraints (12):
    c: Coincident(g0,g-1)
    c: Diameter(g1) = 3.15
    c: Equal(g2,g3)
    c: Equal(g3,g4)
    c: Equal(g4,g1)
    c: DistanceY(g1,g2) = 0
    c: DistanceX(g1,g4) = 0
    c: DistanceY(g3,g4) = 0
    c: DistanceX(g3,g2) = 0
    c: DistanceX(g1,g2) = 20
    c: DistanceY(g3,g2) = 20
    c: Symmetric(g2,g4,g0)
FEATURE [PartDesign::Pocket] Pocket011  label="MountingHoles001"
  BaseFeature = -> Pad024
  Direction = (0,1,-2e-16)
  Length = 6
  Length2 = 5
  Placement = pos=(0,0,0) rot=(1,0,0;1.5708rad)
  Profile = -> Sketch035
  ReferenceAxis = -> Sketch035 [N_Axis]
  Refine = true
  Suppressed = false
  Type = 0
FEATURE [Sketcher::SketchObject] Sketch036
  ArcFitTolerance = 1e-06
  AttachmentSupport = -> [XY_Plane006]
  FullyConstrained = true
  MakeInternals = false
  MapMode = 5
  sketch-geometry (1):
    g0: Circle CenterX=0 CenterY=0 CenterZ=0 NormalX=0 NormalY=0 NormalZ=1 AngleXU=0 Radius=0.25
  constraints (2):
    c: Diameter(g0) = 0.5
    c: Coincident(g0,g-1)
FEATURE [PartDesign::Pad] Pad025
  Direction = (0,0,1)
  Length = 17.3
  Length2 = 10
  Profile = -> Sketch036
  ReferenceAxis = -> Sketch036 [N_Axis]
  Refine = true
  Suppressed = false
  TaperAngle = 15
  Type = 0
FEATURE [Sketcher::SketchObject] Sketch037
  ArcFitTolerance = 1e-06
  AttachmentSupport = -> [Pad025]
  ExternalGeometry = -> [Pad025]
  FullyConstrained = true
  MakeInternals = false
  MapMode = 5
  Placement = pos=(0,0,17.3) rot=(0,0,1;0rad)
  sketch-geometry (1):
    g0: Circle CenterX=0 CenterY=0 CenterZ=0 NormalX=0 NormalY=0 NormalZ=1 AngleXU=0 Radius=4.88552
  constraints (3):
    c: Diameter(g-3) = 9.77104
    c: Coincident(g0,g-1)
    c: Tangent(g0,g-3)
FEATURE [PartDesign::Pad] Pad026
  BaseFeature = -> Pad025
  Direction = (0,0,1)
  Length = 110.7
  Length2 = 10
  Profile = -> Sketch037
  ReferenceAxis = -> Sketch037 [N_Axis]
  Refine = true
  Suppressed = false
  Type = 0
FEATURE [PartDesign::Body] Body006  label="PenPreciseV5"
  AllowCompound = false
  Group = -> [Sketch036,Pad025,Sketch037,Pad026]
  Origin = -> Origin006
  Placement = pos=(-1.1,-53.7,92) rot=(1,0,0;3.14159rad)
  Tip = -> Pad026
FEATURE [Sketcher::SketchObject] Sketch045
  ArcFitTolerance = 1e-06
  FullyConstrained = true
  MakeInternals = false
  MapMode = 5
  Placement = pos=(0,-1e-16,0) rot=(-1,0,0;1.5708rad)
  sketch-geometry (4):
    g0: LineSegment StartX=-37 StartY=-16 StartZ=0 EndX=-37 EndY=-22 EndZ=0
    g1: LineSegment StartX=-37 StartY=-22 StartZ=0 EndX=-17 EndY=-22 EndZ=0
    g2: LineSegment StartX=-17 StartY=-22 StartZ=0 EndX=-17 EndY=-16 EndZ=0
    g3: LineSegment StartX=-17 StartY=-16 StartZ=0 EndX=-37 EndY=-16 EndZ=0
  constraints (11):
    c: Coincident(g0,g1)
    c: Coincident(g1,g2)
    c: Coincident(g2,g3)
    c: Coincident(g3,g0)
    c: Vertical(g0)
    c: Vertical(g2)
    c: Horizontal(g1)
    c: Horizontal(g3)
    c: Distance(g1,g3) = 6
    c: Coincident(g0,g-4)
    c: PointOnObject(g1,g-3)
FEATURE [PartDesign::Pad] Pad030  label="SensorFlange"
  BaseFeature = -> Pocket011
  Direction = (0,1,0)
  Length = 20
  Length2 = 10
  Placement = pos=(0,0,0) rot=(1,0,0;1.5708rad)
  Profile = -> Sketch045
  ReferenceAxis = -> Sketch045 [N_Axis]
  Refine = true
  Suppressed = false
  Type = 0
FEATURE [Sketcher::SketchObject] Sketch046
  ArcFitTolerance = 1e-06
  AttachmentSupport = -> [Pad030]
  ExternalGeometry = -> [Pad030]
  FullyConstrained = true
  MakeInternals = false
  MapMode = 5
  Placement = pos=(0,3.5e-15,16) rot=(1,0,0;3.14159rad)
  sketch-geometry (10):
    g0: GeomPoint [constr] X=-37 Y=-10 Z=0
    g1: GeomPoint [constr] X=-27 Y=-20 Z=0
    g2: LineSegment [constr] StartX=-37 StartY=-20 StartZ=0 EndX=-27 EndY=-20 EndZ=0
    g3: LineSegment [constr] StartX=-27 StartY=-20 StartZ=0 EndX=-27 EndY=-10 EndZ=0
    g4: LineSegment [constr] StartX=-27 StartY=-10 StartZ=0 EndX=-37 EndY=-10 EndZ=0
    g5: LineSegment [constr] StartX=-37 StartY=-10 StartZ=0 EndX=-37 EndY=-20 EndZ=0
    g6: ArcOfCircle CenterX=-27 CenterY=-10 CenterZ=0 NormalX=0 NormalY=0 NormalZ=1 AngleXU=0 Radius=5.95 StartAngle=4e-16 EndAngle=3.14159
    g7: ArcOfCircle CenterX=-27 CenterY=-25 CenterZ=0 NormalX=0 NormalY=0 NormalZ=1 AngleXU=0 Radius=5.95 StartAngle=3.14159 EndAngle=6.28319
    g8: LineSegment StartX=-21.05 StartY=-10 StartZ=0 EndX=-21.05 EndY=-25 EndZ=0
    g9: LineSegment StartX=-32.95 StartY=-10 StartZ=0 EndX=-32.95 EndY=-25 EndZ=0
  constraints (22):
    c: Symmetric(g-4,g-4,g0)
    c: Symmetric(g-3,g-3,g1)
    c: Coincident(g2,g3)
    c: Coincident(g3,g4)
    c: Coincident(g4,g5)
    c: Coincident(g5,g2)
    c: Horizontal(g2)
    c: Horizontal(g4)
    c: Vertical(g3)
    c: Vertical(g5)
    c: Distance(g3,g5) = 10
    c: Distance(g2,g4) = 10
    c: Coincident(g2,g-4)
    c: Tangent(g6,g8) = 1.5708
    c: Tangent(g6,g9) = -1.5708
    c: Tangent(g7,g8) = 1.5708
    c: Tangent(g7,g9) = -1.5708
    c: Equal(g6,g7)
    c: Vertical(g9)
    c: Distance(g6,g7) = 15
    c: Radius(g6) = 5.95
    c: Coincident(g6,g3)
FEATURE [PartDesign::Pocket] Pocket016  label="SensorFlangeSlot"
  BaseFeature = -> Pad030
  Direction = (0,0,1)
  Length = 12
  Length2 = 5
  Placement = pos=(0,0,0) rot=(1,0,0;1.5708rad)
  Profile = -> Sketch046
  ReferenceAxis = -> Sketch046 [N_Axis]
  Refine = true
  Suppressed = false
  Type = 0
FEATURE [Sketcher::SketchObject] Sketch047
  ArcFitTolerance = 1e-06
  AttachmentSupport = -> [Pocket016]
  ExternalGeometry = -> [Pocket016]
  FullyConstrained = true
  MakeInternals = false
  MapMode = 5
  Placement = pos=(0,-6,2.3e-15) rot=(1,0,0;1.5708rad)
  sketch-geometry (3):
    g0: Circle CenterX=10 CenterY=-4 CenterZ=0 NormalX=0 NormalY=0 NormalZ=1 AngleXU=0 Radius=1.6
    g1: Circle CenterX=10 CenterY=4 CenterZ=0 NormalX=0 NormalY=0 NormalZ=1 AngleXU=0 Radius=1.6
    g2: Circle CenterX=-10 CenterY=0 CenterZ=0 NormalX=0 NormalY=0 NormalZ=1 AngleXU=0 Radius=1.6
  constraints (8):
    c: Diameter(g1) = 3.2
    c: Equal(g2,g1)
    c: Equal(g1,g0)
    c: PointOnObject(g2,g-1)
    c: DistanceX(g-3,g1) = 0
    c: DistanceY(g0,g1) = 8
    c: DistanceX(g2,g-1) = 10
    c: Symmetric(g0,g1,g-1)
FEATURE [PartDesign::Pocket] Pocket017  label="AlignmentDowelHoles"
  BaseFeature = -> Pocket016
  Direction = (0,1,-2e-16)
  Length = 6
  Length2 = 5
  Placement = pos=(0,0,0) rot=(1,0,0;1.5708rad)
  Profile = -> Sketch047
  ReferenceAxis = -> Sketch047 [N_Axis]
  Refine = true
  Suppressed = false
  Type = 0
FEATURE [Sketcher::SketchObject] Sketch048
  ArcFitTolerance = 1e-06
  AttachmentSupport = -> [Pocket017]
  ExternalGeometry = -> [Pocket017]
  FullyConstrained = true
  MakeInternals = false
  MapMode = 5
  Placement = pos=(0,-6,2.3e-15) rot=(1,0,0;1.5708rad)
  sketch-geometry (4):
    g0: Circle CenterX=-10 CenterY=10 CenterZ=0 NormalX=0 NormalY=0 NormalZ=1 AngleXU=0 Radius=3
    g1: Circle CenterX=10 CenterY=10 CenterZ=0 NormalX=0 NormalY=0 NormalZ=1 AngleXU=0 Radius=3
    g2: Circle CenterX=10 CenterY=-10 CenterZ=0 NormalX=0 NormalY=0 NormalZ=1 AngleXU=0 Radius=3
    g3: Circle CenterX=-10 CenterY=-10 CenterZ=0 NormalX=0 NormalY=0 NormalZ=1 AngleXU=0 Radius=3
  constraints (8):
    c: Diameter(g0) = 6
    c: Coincident(g0,g-3)
    c: Coincident(g1,g-4)
    c: Coincident(g2,g-5)
    c: Coincident(g3,g-6)
    c: Equal(g1,g0)
    c: Equal(g0,g3)
    c: Equal(g3,g2)
FEATURE [PartDesign::Pocket] Pocket018  label="TableMountScrewCapInset"
  BaseFeature = -> Pocket017
  Direction = (0,1,-2e-16)
  Length = 2.5
  Length2 = 5
  Placement = pos=(0,0,0) rot=(1,0,0;1.5708rad)
  Profile = -> Sketch048
  ReferenceAxis = -> Sketch048 [N_Axis]
  Refine = true
  Suppressed = false
  Type = 0
FEATURE [Sketcher::SketchObject] Sketch049
  ArcFitTolerance = 1e-06
  AttachmentSupport = -> [Pocket018]
  ExternalGeometry = -> [Pocket018]
  FullyConstrained = true
  MakeInternals = false
  MapMode = 5
  Placement = pos=(0,3e-16,0) rot=(-1,0,0;1.5708rad)
  sketch-geometry (3):
    g0: Circle CenterX=-10 CenterY=0 CenterZ=0 NormalX=0 NormalY=0 NormalZ=1 AngleXU=0 Radius=3
    g1: Circle CenterX=10 CenterY=4 CenterZ=0 NormalX=0 NormalY=0 NormalZ=1 AngleXU=0 Radius=3
    g2: Circle CenterX=10 CenterY=-4 CenterZ=0 NormalX=0 NormalY=0 NormalZ=1 AngleXU=0 Radius=3
  constraints (6):
    c: Diameter(g0) = 6
    c: Coincident(g0,g-5)
    c: Coincident(g1,g-3)
    c: Coincident(g2,g-4)
    c: Equal(g2,g1)
    c: Equal(g1,g0)
FEATURE [PartDesign::Pocket] Pocket019  label="AlignmentDowelScrewCapInset"
  BaseFeature = -> Pocket018
  Direction = (0,-1,-2e-16)
  Length = 2.5
  Length2 = 5
  Placement = pos=(0,0,0) rot=(1,0,0;1.5708rad)
  Profile = -> Sketch049
  ReferenceAxis = -> Sketch049 [N_Axis]
  Refine = true
  Suppressed = false
  Type = 0
FEATURE [Sketcher::SketchObject] Sketch050
  ArcFitTolerance = 1e-06
  AttachmentSupport = -> [XZ_Plane007]
  FullyConstrained = true
  MakeInternals = false
  MapMode = 5
  Placement = pos=(0,0,0) rot=(1,0,0;1.5708rad)
  sketch-geometry (1):
    g0: Circle CenterX=0 CenterY=0 CenterZ=0 NormalX=0 NormalY=0 NormalZ=1 AngleXU=0 Radius=2.5
  constraints (2):
    c: Diameter(g0) = 5
    c: Coincident(g0,g-1)
FEATURE [PartDesign::Pad] Pad031  label="Head"
  Direction = (0,-1,2e-16)
  Length = 2.1
  Length2 = 10
  Placement = pos=(0,0,0) rot=(1,0,0;1.5708rad)
  Profile = -> Sketch050
  ReferenceAxis = -> Sketch050 [N_Axis]
  Refine = true
  Suppressed = false
  Type = 0
FEATURE [Sketcher::SketchObject] Sketch051
  ArcFitTolerance = 1e-06
  AttachmentSupport = -> [Pad031]
  FullyConstrained = true
  MakeInternals = false
  MapMode = 5
  Placement = pos=(0,-2.1,0) rot=(1,0,0;1.5708rad)
  sketch-geometry (1):
    g0: Circle CenterX=0 CenterY=0 CenterZ=0 NormalX=0 NormalY=0 NormalZ=1 AngleXU=0 Radius=1.5
  constraints (2):
    c: Coincident(g0,g-1)
    c: Diameter(g0) = 3
FEATURE [PartDesign::Pad] Pad032
  BaseFeature = -> Pad031
  Direction = (0,-1,2e-16)
  Length = 20
  Length2 = 10
  Placement = pos=(0,0,0) rot=(1,0,0;1.5708rad)
  Profile = -> Sketch051
  ReferenceAxis = -> Sketch051 [N_Axis]
  Refine = true
  Suppressed = false
  Type = 0
FEATURE [PartDesign::Body] Body007  label="AlignmentDowelScrew"
  AllowCompound = false
  Group = -> [Sketch050,Pad031,Sketch051,Pad032]
  Origin = -> Origin007
  Placement = pos=(9,-37.4,35.4) rot=(0,0,1;0rad)
  Tip = -> Pad032
FEATURE [Sketcher::SketchObject] Sketch052
  ArcFitTolerance = 1e-06
  AttachmentSupport = -> [XZ_Plane008]
  FullyConstrained = true
  MakeInternals = false
  MapMode = 5
  Placement = pos=(0,0,0) rot=(1,0,0;1.5708rad)
  sketch-geometry (1):
    g0: Circle CenterX=0 CenterY=0 CenterZ=0 NormalX=0 NormalY=0 NormalZ=1 AngleXU=0 Radius=2.5
  constraints (2):
    c: Diameter(g0) = 5
    c: Coincident(g0,g-1)
FEATURE [PartDesign::Pad] Pad033  label="Head001"
  Direction = (0,-1,2e-16)
  Length = 2.1
  Length2 = 10
  Placement = pos=(0,0,0) rot=(1,0,0;1.5708rad)
  Profile = -> Sketch052
  ReferenceAxis = -> Sketch052 [N_Axis]
  Refine = true
  Suppressed = false
  Type = 0
FEATURE [Sketcher::SketchObject] Sketch053
  ArcFitTolerance = 1e-06
  AttachmentSupport = -> [Pad033]
  FullyConstrained = true
  MakeInternals = false
  MapMode = 5
  Placement = pos=(0,-2.1,0) rot=(1,0,0;1.5708rad)
  sketch-geometry (1):
    g0: Circle CenterX=0 CenterY=0 CenterZ=0 NormalX=0 NormalY=0 NormalZ=1 AngleXU=0 Radius=1.5
  constraints (2):
    c: Coincident(g0,g-1)
    c: Diameter(g0) = 3
FEATURE [PartDesign::Pad] Pad034
  BaseFeature = -> Pad033
  Direction = (0,-1,2e-16)
  Length = 20
  Length2 = 10
  Placement = pos=(0,0,0) rot=(1,0,0;1.5708rad)
  Profile = -> Sketch053
  ReferenceAxis = -> Sketch053 [N_Axis]
  Refine = true
  Suppressed = false
  Type = 0
FEATURE [PartDesign::Body] Body008  label="AlignmentDowelScrew001"
  AllowCompound = false
  Group = -> [Sketch052,Pad033,Sketch053,Pad034]
  Origin = -> Origin008
  Placement = pos=(9,-37,43.4) rot=(0,0,1;0rad)
  Tip = -> Pad034
FEATURE [Sketcher::SketchObject] Sketch054
  ArcFitTolerance = 1e-06
  AttachmentSupport = -> [XZ_Plane009]
  FullyConstrained = true
  MakeInternals = false
  MapMode = 5
  Placement = pos=(0,0,0) rot=(1,0,0;1.5708rad)
  sketch-geometry (1):
    g0: Circle CenterX=0 CenterY=0 CenterZ=0 NormalX=0 NormalY=0 NormalZ=1 AngleXU=0 Radius=2.5
  constraints (2):
    c: Diameter(g0) = 5
    c: Coincident(g0,g-1)
FEATURE [PartDesign::Pad] Pad035  label="Head002"
  Direction = (0,-1,2e-16)
  Length = 2.1
  Length2 = 10
  Placement = pos=(0,0,0) rot=(1,0,0;1.5708rad)
  Profile = -> Sketch054
  ReferenceAxis = -> Sketch054 [N_Axis]
  Refine = true
  Suppressed = false
  Type = 0
FEATURE [Sketcher::SketchObject] Sketch055
  ArcFitTolerance = 1e-06
  AttachmentSupport = -> [Pad035]
  FullyConstrained = true
  MakeInternals = false
  MapMode = 5
  Placement = pos=(0,-2.1,0) rot=(1,0,0;1.5708rad)
  sketch-geometry (1):
    g0: Circle CenterX=0 CenterY=0 CenterZ=0 NormalX=0 NormalY=0 NormalZ=1 AngleXU=0 Radius=1.5
  constraints (2):
    c: Coincident(g0,g-1)
    c: Diameter(g0) = 3
FEATURE [PartDesign::Pad] Pad036
  BaseFeature = -> Pad035
  Direction = (0,-1,2e-16)
  Length = 20
  Length2 = 10
  Placement = pos=(0,0,0) rot=(1,0,0;1.5708rad)
  Profile = -> Sketch055
  ReferenceAxis = -> Sketch055 [N_Axis]
  Refine = true
  Suppressed = false
  Type = 0
FEATURE [PartDesign::Body] Body009  label="AlignmentDowelScrew002"
  AllowCompound = false
  Group = -> [Sketch054,Pad035,Sketch055,Pad036]
  Origin = -> Origin009
  Placement = pos=(-11,-38,39.4) rot=(0,0,1;0rad)
  Tip = -> Pad036
FEATURE [Sketcher::SketchObject] Sketch056
  ArcFitTolerance = 1e-06
  AttachmentSupport = -> [XZ_Plane010]
  FullyConstrained = true
  MakeInternals = false
  MapMode = 5
  Placement = pos=(0,0,0) rot=(1,0,0;1.5708rad)
  sketch-geometry (8):
    g0: LineSegment StartX=-15 StartY=-16 StartZ=0 EndX=15 EndY=-16 EndZ=0
    g1: LineSegment StartX=15 StartY=-16 StartZ=0 EndX=15 EndY=16 EndZ=0
    g2: LineSegment StartX=15 StartY=16 StartZ=0 EndX=-15 EndY=16 EndZ=0
    g3: LineSegment StartX=-15 StartY=16 StartZ=0 EndX=-15 EndY=-16 EndZ=0
    g4: GeomPoint [constr] X=0 Y=0 Z=0
    g5: Circle CenterX=10 CenterY=4 CenterZ=0 NormalX=0 NormalY=0 NormalZ=1 AngleXU=0 Radius=1.7
    g6: Circle CenterX=10 CenterY=-4 CenterZ=0 NormalX=0 NormalY=0 NormalZ=1 AngleXU=0 Radius=1.7
    g7: Circle CenterX=-10 CenterY=0 CenterZ=0 NormalX=0 NormalY=0 NormalZ=1 AngleXU=0 Radius=1.7
  constraints (21):
    c: Coincident(g0,g1)
    c: Coincident(g1,g2)
    c: Coincident(g2,g3)
    c: Coincident(g3,g0)
    c: Horizontal(g0)
    c: Horizontal(g2)
    c: Vertical(g1)
    c: Vertical(g3)
    c: Symmetric(g2,g0,g4)
    c: Distance(g1,g3) = 30
    c: Distance(g0,g2) = 32
    c: Coincident(g4,g-1)
    c: Diameter(g5) = 3.4
    c: PointOnObject(g7,g-1)
    c: Equal(g7,g6)
    c: Equal(g6,g5)
    c: DistanceX(g6,g5) = 0
    c: DistanceY(g6,g5) = 8
    c: DistanceY(g7,g5) = 4
    c: DistanceX(g7,g5) = 20
    c: DistanceX(g7,g4) = 10
FEATURE [PartDesign::Pad] Pad037  label="PenToolAndAlignmentHoles"
  Direction = (0,-1,2e-16)
  Length = 10
  Length2 = 10
  Placement = pos=(0,0,0) rot=(1,0,0;1.5708rad)
  Profile = -> Sketch056
  ReferenceAxis = -> Sketch056 [N_Axis]
  Refine = true
  Suppressed = false
  Type = 0
FEATURE [Sketcher::SketchObject] Sketch057
  ArcFitTolerance = 1e-06
  AttachmentSupport = -> [Pad037]
  ExternalGeometry = -> [Pad037]
  FullyConstrained = true
  MakeInternals = false
  MapMode = 5
  Placement = pos=(0,0,0) rot=(-1,0,0;1.5708rad)
  sketch-geometry (3):
    g0: Circle CenterX=-10 CenterY=0 CenterZ=0 NormalX=0 NormalY=0 NormalZ=1 AngleXU=0 Radius=3.5
    g1: Circle CenterX=10 CenterY=4 CenterZ=0 NormalX=0 NormalY=0 NormalZ=1 AngleXU=0 Radius=3.5
    g2: Circle CenterX=10 CenterY=-4 CenterZ=0 NormalX=0 NormalY=0 NormalZ=1 AngleXU=0 Radius=3.5
  constraints (6):
    c: Coincident(g0,g-3)
    c: Coincident(g1,g-4)
    c: Coincident(g2,g-5)
    c: Diameter(g0) = 7
    c: Equal(g1,g2)
    c: Equal(g2,g0)
FEATURE [PartDesign::Pocket] Pocket020  label="AlignmentHoleCones"
  BaseFeature = -> Pad037
  Direction = (0,-1,-2e-16)
  Length = 5
  Length2 = 5
  Placement = pos=(0,0,0) rot=(1,0,0;1.5708rad)
  Profile = -> Sketch057
  ReferenceAxis = -> Sketch057 [N_Axis]
  Refine = true
  Suppressed = false
  TaperAngle = -20
  Type = 0
FEATURE [Sketcher::SketchObject] Sketch059
  ArcFitTolerance = 1e-06
  AttachmentSupport = -> [Pocket020]
  ExternalGeometry = -> [Pocket020]
  FullyConstrained = true
  MakeInternals = false
  MapMode = 5
  Placement = pos=(0,-7e-15,-16) rot=(1,0,0;3.14159rad)
  sketch-geometry (1):
    g0: Circle CenterX=0 CenterY=10 CenterZ=0 NormalX=0 NormalY=0 NormalZ=1 AngleXU=0 Radius=4.925
  constraints (2):
    c: Diameter(g0) = 9.85
    c: Symmetric(g-3,g-3,g0)
FEATURE [PartDesign::Pocket] Pocket022  label="PenSlot"
  BaseFeature = -> Pocket020
  Direction = (0,0,1)
  Length = 32
  Length2 = 5
  Placement = pos=(0,0,0) rot=(1,0,0;1.5708rad)
  Profile = -> Sketch059
  ReferenceAxis = -> Sketch059 [N_Axis]
  Refine = true
  Suppressed = false
  Type = 0
FEATURE [Sketcher::SketchObject] Sketch060
  ArcFitTolerance = 1e-06
  AttachmentSupport = -> [Pocket022]
  ExternalGeometry = -> [Pocket022]
  FullyConstrained = true
  MakeInternals = false
  MapMode = 5
  Placement = pos=(15,0,0) rot=(0.707107,0,0.707107;3.14159rad)
  sketch-geometry (4):
    g0: LineSegment StartX=16 StartY=0 StartZ=0 EndX=16 EndY=10 EndZ=0
    g1: LineSegment StartX=16 StartY=10 StartZ=0 EndX=-16 EndY=10 EndZ=0
    g2: LineSegment StartX=-16 StartY=10 StartZ=0 EndX=-16 EndY=0 EndZ=0
    g3: LineSegment StartX=-16 StartY=0 StartZ=0 EndX=16 EndY=0 EndZ=0
  constraints (10):
    c: Coincident(g0,g1)
    c: Coincident(g1,g2)
    c: Coincident(g2,g3)
    c: Coincident(g3,g0)
    c: Vertical(g0)
    c: Vertical(g2)
    c: Horizontal(g1)
    c: Horizontal(g3)
    c: Coincident(g0,g-3)
    c: Coincident(g1,g-4)
FEATURE [PartDesign::Pad] Pad038  label="MagnetHolderExtension"
  BaseFeature = -> Pocket022
  Direction = (1,0,-2e-16)
  Length = 12
  Length2 = 10
  Placement = pos=(0,0,0) rot=(1,0,0;1.5708rad)
  Profile = -> Sketch060
  ReferenceAxis = -> Sketch060 [N_Axis]
  Refine = true
  Suppressed = false
  Type = 0
FEATURE [Sketcher::SketchObject] Sketch062
  ArcFitTolerance = 1e-06
  FullyConstrained = true
  MakeInternals = false
  MapMode = 5
  Placement = pos=(0,-10,4e-16) rot=(1,0,0;1.5708rad)
  sketch-geometry (4):
    g0: Circle CenterX=-10 CenterY=10 CenterZ=0 NormalX=0 NormalY=0 NormalZ=1 AngleXU=0 Radius=1.575
    g1: Circle CenterX=-10 CenterY=-10 CenterZ=0 NormalX=0 NormalY=0 NormalZ=1 AngleXU=0 Radius=1.575
    g2: Circle CenterX=10 CenterY=10 CenterZ=0 NormalX=0 NormalY=0 NormalZ=1 AngleXU=0 Radius=1.575
    g3: Circle CenterX=10 CenterY=-10 CenterZ=0 NormalX=0 NormalY=0 NormalZ=1 AngleXU=0 Radius=1.575
  constraints (9):
    c: Equal(g3,g2)
    c: Equal(g2,g0)
    c: Equal(g0,g1)
    c: Symmetric(g0,g1,g-1)
    c: Symmetric(g2,g3,g-1)
    c: DistanceX(g1,g3) = 20
    c: DistanceY(g3,g2) = 20
    c: Symmetric(g2,g0,g-2)
    c: Diameter(g3) = 3.15
FEATURE [PartDesign::Pocket] Pocket024  label="PenRetainerHoles"
  BaseFeature = -> Pad038
  Direction = (0,1,0)
  Length = 8
  Length2 = 5
  Placement = pos=(0,0,0) rot=(1,0,0;1.5708rad)
  Profile = -> Sketch062
  ReferenceAxis = -> Sketch062 [N_Axis]
  Refine = true
  Suppressed = false
  Type = 0
FEATURE [Sketcher::SketchObject] Sketch063
  ArcFitTolerance = 1e-06
  AttachmentSupport = -> [XZ_Plane011]
  FullyConstrained = false
  MakeInternals = false
  MapMode = 5
  Placement = pos=(0,0,0) rot=(1,0,0;1.5708rad)
  sketch-geometry (8):
    g0: LineSegment StartX=-15 StartY=-16 StartZ=0 EndX=15 EndY=-16 EndZ=0
    g1: LineSegment StartX=15 StartY=16 StartZ=0 EndX=-15 EndY=16 EndZ=0
    g2: LineSegment StartX=-15 StartY=16 StartZ=0 EndX=-15 EndY=-16 EndZ=0
    g3: GeomPoint [constr] X=0 Y=0 Z=0
    g4: Circle CenterX=-10 CenterY=0 CenterZ=0 NormalX=0 NormalY=0 NormalZ=1 AngleXU=0 Radius=1.75
    g5: Circle CenterX=10 CenterY=4 CenterZ=0 NormalX=0 NormalY=0 NormalZ=1 AngleXU=0 Radius=1.75
    g6: Circle CenterX=10 CenterY=-4 CenterZ=0 NormalX=0 NormalY=0 NormalZ=1 AngleXU=0 Radius=1.75
    g7: LineSegment StartX=15 StartY=16 StartZ=0 EndX=15 EndY=-16 EndZ=0
  constraints (19):
    c: Coincident(g1,g2)
    c: Coincident(g2,g0)
    c: Horizontal(g0)
    c: Horizontal(g1)
    c: Vertical(g2)
    c: Distance(g0,g2) = 30
    c: Distance(g0,g1) = 32
    c: Coincident(g3,g-1)
    c: PointOnObject(g4,g-1)
    c: Equal(g6,g5)
    c: Equal(g5,g4)
    c: Diameter(g4) = 3.5
    c: DistanceX(g4,g3) = 10
    c: DistanceY(g6,g5) = 8
    c: Symmetric(g5,g6,g-1)
    c: DistanceX(g3,g5) = 10
    c: Coincident(g1,g7)
    c: Coincident(g7,g0)
    c: Vertical(g7)
FEATURE [PartDesign::Pad] Pad039  label="BaseAndAlignmentDowelHoles"
  Direction = (0,-1,2e-16)
  Length = 8
  Length2 = 10
  Placement = pos=(0,0,0) rot=(1,0,0;1.5708rad)
  Profile = -> Sketch063
  ReferenceAxis = -> Sketch063 [N_Axis]
  Refine = true
  Suppressed = false
  Type = 0
FEATURE [Sketcher::SketchObject] Sketch064
  ArcFitTolerance = 1e-06
  AttachmentSupport = -> [Pad039]
  FullyConstrained = true
  MakeInternals = false
  MapMode = 5
  Placement = pos=(0,-7e-15,-16) rot=(1,0,0;3.14159rad)
  sketch-geometry (1):
    g0: Circle CenterX=0 CenterY=0 CenterZ=0 NormalX=0 NormalY=0 NormalZ=1 AngleXU=0 Radius=4.925
  constraints (2):
    c: Diameter(g0) = 9.85
    c: Coincident(g0,g-1)
FEATURE [PartDesign::Pocket] Pocket025  label="PenSlot001"
  BaseFeature = -> Pad039
  Direction = (0,0,1)
  Length = 38
  Length2 = 5
  Placement = pos=(0,0,0) rot=(1,0,0;1.5708rad)
  Profile = -> Sketch064
  ReferenceAxis = -> Sketch064 [N_Axis]
  Refine = true
  Suppressed = false
  Type = 0
FEATURE [Sketcher::SketchObject] Sketch065
  ArcFitTolerance = 1e-06
  AttachmentSupport = -> [Pocket025]
  ExternalGeometry = -> [Pocket025]
  FullyConstrained = true
  MakeInternals = false
  MapMode = 5
  Placement = pos=(0,0,0) rot=(-1,0,0;1.5708rad)
  sketch-geometry (11):
    g0: Circle CenterX=26.925 CenterY=5 CenterZ=0 NormalX=0 NormalY=0 NormalZ=1 AngleXU=0 Radius=1.6
    g1: LineSegment [constr] StartX=4.925 StartY=16 StartZ=0 EndX=38.925 EndY=16 EndZ=0
    g2: LineSegment [constr] StartX=-10 StartY=-10 StartZ=0 EndX=10 EndY=-10 EndZ=0
    g3: LineSegment [constr] StartX=10 StartY=-10 StartZ=0 EndX=10 EndY=10 EndZ=0
    g4: LineSegment [constr] StartX=10 StartY=10 StartZ=0 EndX=-10 EndY=10 EndZ=0
    g5: LineSegment [constr] StartX=-10 StartY=10 StartZ=0 EndX=-10 EndY=-10 EndZ=0
    g6: GeomPoint [constr] X=0 Y=0 Z=0
    g7: Circle CenterX=-10 CenterY=10 CenterZ=0 NormalX=0 NormalY=0 NormalZ=1 AngleXU=0 Radius=1.6
    g8: Circle CenterX=10 CenterY=10 CenterZ=0 NormalX=0 NormalY=0 NormalZ=1 AngleXU=0 Radius=1.6
    g9: Circle CenterX=10 CenterY=-10 CenterZ=0 NormalX=0 NormalY=0 NormalZ=1 AngleXU=0 Radius=1.6
    g10: Circle CenterX=-10 CenterY=-10 CenterZ=0 NormalX=0 NormalY=0 NormalZ=1 AngleXU=0 Radius=1.6
  constraints (26):
    c: Diameter(g0) = 3.2
    c: DistanceY(g0,g-3) = 11
    c: Distance(g1) = 34
    c: Horizontal(g1)
    c: DistanceX(g0,g1) = 12
    c: Coincident(g1,g-3)
    c: Coincident(g2,g3)
    c: Coincident(g3,g4)
    c: Coincident(g4,g5)
    c: Coincident(g5,g2)
    c: Horizontal(g2)
    c: Horizontal(g4)
    c: Vertical(g3)
    c: Vertical(g5)
    c: Symmetric(g4,g2,g6)
    c: Distance(g3,g5) = 20
    c: Distance(g2,g4) = 20
    c: Coincident(g6,g-1)
    c: Diameter(g7) = 3.2
    c: Coincident(g8,g3)
    c: Coincident(g9,g2)
    c: Coincident(g10,g2)
    c: Equal(g9,g8)
    c: Equal(g8,g10)
    c: Equal(g10,g7)
    c: Coincident(g7,g4)
FEATURE [PartDesign::Pocket] Pocket026  label="PenRetainerHoles001"
  BaseFeature = -> Pocket025
  Direction = (0,-1,-2e-16)
  Length = 10
  Length2 = 5
  Placement = pos=(0,0,0) rot=(1,0,0;1.5708rad)
  Profile = -> Sketch065
  ReferenceAxis = -> Sketch065 [N_Axis]
  Refine = true
  Suppressed = false
  Type = 0
FEATURE [PartDesign::Body] Body011  label="PenRetainer"
  AllowCompound = false
  Group = -> [Sketch063,Pad039,Sketch064,Pocket025,Sketch065,Pocket026]
  Origin = -> Origin011
  Placement = pos=(-1.1,-53.7,39.5) rot=(0,0,1;0rad)
  Tip = -> Pocket026
FEATURE [Sketcher::SketchObject] Sketch066
  ArcFitTolerance = 1e-06
  AttachmentSupport = -> [Pocket010]
  ExternalGeometry = -> [Pocket010]
  FullyConstrained = true
  MakeInternals = false
  MapMode = 5
  Placement = pos=(-32,0,0) rot=(0.707107,0,-0.707107;3.14159rad)
  sketch-geometry (4):
    g0: LineSegment StartX=-39 StartY=0 StartZ=0 EndX=-22.2 EndY=0 EndZ=0
    g1: LineSegment StartX=-22.2 StartY=0 StartZ=0 EndX=-22.2 EndY=9 EndZ=0
    g2: LineSegment StartX=-22.2 StartY=9 StartZ=0 EndX=-39 EndY=9 EndZ=0
    g3: LineSegment StartX=-39 StartY=9 StartZ=0 EndX=-39 EndY=0 EndZ=0
  constraints (12):
    c: Coincident(g0,g1)
    c: Coincident(g1,g2)
    c: Coincident(g2,g3)
    c: Coincident(g3,g0)
    c: Horizontal(g0)
    c: Horizontal(g2)
    c: Vertical(g1)
    c: Vertical(g3)
    c: Distance(g1,g3) = 16.8
    c: PointOnObject(g1,g-5)
    c: DistanceX(g0,g-4) = 7
    c: PointOnObject(g0,g-4)
FEATURE [PartDesign::Pad] Pad040  label="XLimitSwitchLeftExtension1"
  BaseFeature = -> Pocket010
  Direction = (-1,0,-2e-16)
  Length = 8
  Length2 = 10
  Placement = pos=(0,0,0) rot=(1,0,0;1.5708rad)
  Profile = -> Sketch066
  ReferenceAxis = -> Sketch066 [N_Axis]
  Refine = true
  Suppressed = false
  Type = 0
FEATURE [PartDesign::Pad] Pad041  label="XLimitSwitchLeftExtension2"
  BaseFeature = -> Pad040
  Direction = (0,4e-16,1)
  Length = 7
  Length2 = 10
  Placement = pos=(0,0,0) rot=(1,0,0;1.5708rad)
  Profile = -> Pad040 [Face8]
  Refine = true
  Suppressed = false
  Type = 0
FEATURE [PartDesign::Mirrored] Mirrored  label="XLimitSwitchRightExtension1"
  BaseFeature = -> Pad041
  MirrorPlane = -> YZ_Plane
  Originals = -> [Pad040]
  Placement = pos=(0,0,0) rot=(1,0,0;1.5708rad)
  Refine = true
  Suppressed = false
  TransformMode = 0
FEATURE [PartDesign::Pad] Pad042  label="XLimitSwitchRightExtension2"
  BaseFeature = -> Mirrored
  Direction = (0,4e-16,1)
  Length = 7
  Length2 = 10
  Placement = pos=(0,0,0) rot=(1,0,0;1.5708rad)
  Profile = -> Mirrored [Face11]
  Refine = true
  Suppressed = false
  Type = 0
FEATURE [Sketcher::SketchObject] Sketch067
  ArcFitTolerance = 1e-06
  AttachmentSupport = -> [Pad042]
  ExternalGeometry = -> [Pad042]
  FullyConstrained = true
  MakeInternals = false
  MapMode = 5
  Placement = pos=(0,-9,2.8e-15) rot=(1,0,0;1.5708rad)
  sketch-geometry (8):
    g0: LineSegment StartX=40 StartY=39 StartZ=0 EndX=32 EndY=39 EndZ=0
    g1: LineSegment StartX=32 StartY=39 StartZ=0 EndX=32 EndY=22.2 EndZ=0
    g2: LineSegment StartX=32 StartY=22.2 StartZ=0 EndX=40 EndY=22.2 EndZ=0
    g3: LineSegment StartX=40 StartY=22.2 StartZ=0 EndX=40 EndY=24.2 EndZ=0
    g4: LineSegment StartX=40 StartY=24.2 StartZ=0 EndX=34 EndY=24.2 EndZ=0
    g5: LineSegment StartX=34 StartY=24.2 StartZ=0 EndX=34 EndY=37 EndZ=0
    g6: LineSegment StartX=34 StartY=37 StartZ=0 EndX=40 EndY=37 EndZ=0
    g7: LineSegment StartX=40 StartY=37 StartZ=0 EndX=40 EndY=39 EndZ=0
  constraints (23):
    c: PointOnObject(g0,g-4)
    c: Horizontal(g0)
    c: Coincident(g0,g1)
    c: Vertical(g1)
    c: Coincident(g1,g2)
    c: Horizontal(g2)
    c: Coincident(g2,g3)
    c: PointOnObject(g3,g-4)
    c: Coincident(g3,g4)
    c: Horizontal(g4)
    c: Coincident(g4,g5)
    c: Vertical(g5)
    c: Coincident(g5,g6)
    c: PointOnObject(g6,g-4)
    c: Horizontal(g6)
    c: Coincident(g6,g7)
    c: Coincident(g7,g0)
    c: DistanceY(g5,g5) = 12.8
    c: DistanceY(g7,g7) = 2
    c: Equal(g3,g7)
    c: DistanceX(g0,g5) = 2
    c: Coincident(g2,g-5)
    c: DistanceX(g4,g4) = 6
FEATURE [PartDesign::Pad] Pad043  label="XLimitSwitchLeftSlot"
  BaseFeature = -> Pad042
  Direction = (0,-1,2e-16)
  Length = 5.8
  Length2 = 10
  Placement = pos=(0,0,0) rot=(1,0,0;1.5708rad)
  Profile = -> Sketch067
  ReferenceAxis = -> Sketch067 [N_Axis]
  Refine = true
  Suppressed = false
  Type = 0
FEATURE [PartDesign::Mirrored] Mirrored001  label="XLimitSwitchRightSlot"
  BaseFeature = -> Pad043
  MirrorPlane = -> YZ_Plane
  Originals = -> [Pad043]
  Placement = pos=(0,0,0) rot=(1,0,0;1.5708rad)
  Refine = true
  Suppressed = false
  TransformMode = 0
FEATURE [Sketcher::SketchObject] Sketch068
  ArcFitTolerance = 1e-06
  AttachmentSupport = -> [Mirrored001]
  ExternalGeometry = -> [Mirrored001]
  FullyConstrained = true
  MakeInternals = false
  MapMode = 5
  Placement = pos=(-34,7.5e-15,-7.5e-15) rot=(0.707107,0,-0.707107;3.14159rad)
  sketch-geometry (1):
    g0: Circle CenterX=-24.2 CenterY=11.9 CenterZ=0 NormalX=0 NormalY=0 NormalZ=1 AngleXU=0 Radius=2
  constraints (2):
    c: Diameter(g0) = 4
    c: Symmetric(g-4,g-4,g0)
FEATURE [PartDesign::Pocket] Pocket027  label="XLimitSwitchLeftPinHole"
  BaseFeature = -> Mirrored001
  Direction = (1,0,2e-16)
  Length = 5
  Length2 = 5
  Placement = pos=(0,0,0) rot=(1,0,0;1.5708rad)
  Profile = -> Sketch068
  ReferenceAxis = -> Sketch068 [N_Axis]
  Refine = true
  Suppressed = false
  Type = 0
FEATURE [PartDesign::LinearPattern] LinearPattern  label="XLimitSwitchLeftPinHoles"
  BaseFeature = -> Pocket027
  Direction = -> Sketch068 [H_Axis]
  Length = 12.8
  Mode = 0
  Occurrences = 3
  Offset = 6.4
  Originals = -> [Pocket027]
  Placement = pos=(0,0,0) rot=(1,0,0;1.5708rad)
  Refine = true
  Reversed = true
  Suppressed = false
  TransformMode = 0
FEATURE [Sketcher::SketchObject] Sketch069
  ArcFitTolerance = 1e-06
  AttachmentSupport = -> [LinearPattern]
  ExternalGeometry = -> [LinearPattern]
  FullyConstrained = true
  MakeInternals = false
  MapMode = 5
  Placement = pos=(34,0,0) rot=(0.707107,0,0.707107;3.14159rad)
  sketch-geometry (1):
    g0: Circle CenterX=37 CenterY=11.9 CenterZ=0 NormalX=0 NormalY=0 NormalZ=1 AngleXU=0 Radius=2
  constraints (2):
    c: Diameter(g0) = 4
    c: Symmetric(g-4,g-4,g0)
FEATURE [PartDesign::Pocket] Pocket028  label="XLimitSwitchRightPinHole"
  BaseFeature = -> LinearPattern
  Direction = (-1,0,2e-16)
  Length = 5
  Length2 = 5
  Placement = pos=(0,0,0) rot=(1,0,0;1.5708rad)
  Profile = -> Sketch069
  ReferenceAxis = -> Sketch069 [N_Axis]
  Refine = true
  Suppressed = false
  Type = 0
FEATURE [PartDesign::LinearPattern] LinearPattern001  label="XLimitSwitchRightPinHoles"
  BaseFeature = -> Pocket028
  Direction = -> Sketch069 [H_Axis]
  Length = 12.8
  Mode = 0
  Occurrences = 3
  Offset = 6.4
  Originals = -> [Pocket028]
  Placement = pos=(0,0,0) rot=(1,0,0;1.5708rad)
  Refine = true
  Reversed = true
  Suppressed = false
  TransformMode = 0
FEATURE [Sketcher::SketchObject] Sketch071
  ArcFitTolerance = 1e-06
  AttachmentSupport = -> [LinearPattern001]
  ExternalGeometry = -> [LinearPattern001]
  FullyConstrained = true
  MakeInternals = false
  MapMode = 5
  Placement = pos=(0,-9,2.8e-15) rot=(1,0,0;1.5708rad)
  sketch-geometry (8):
    g0: LineSegment StartX=30 StartY=19.7 StartZ=0 EndX=30 EndY=23.7 EndZ=0
    g1: LineSegment StartX=30 StartY=23.7 StartZ=0 EndX=20 EndY=23.7 EndZ=0
    g2: LineSegment StartX=20 StartY=23.7 StartZ=0 EndX=20 EndY=19.7 EndZ=0
    g3: LineSegment StartX=20 StartY=19.7 StartZ=0 EndX=30 EndY=19.7 EndZ=0
    g4: LineSegment StartX=30 StartY=-26.3 StartZ=0 EndX=20 EndY=-26.3 EndZ=0
    g5: LineSegment StartX=20 StartY=-26.3 StartZ=0 EndX=20 EndY=-30.3 EndZ=0
    g6: LineSegment StartX=20 StartY=-30.3 StartZ=0 EndX=30 EndY=-30.3 EndZ=0
    g7: LineSegment StartX=30 StartY=-30.3 StartZ=0 EndX=30 EndY=-26.3 EndZ=0
  constraints (24):
    c: Coincident(g0,g1)
    c: Coincident(g1,g2)
    c: Coincident(g2,g3)
    c: Coincident(g3,g0)
    c: Vertical(g0)
    c: Vertical(g2)
    c: Horizontal(g1)
    c: Horizontal(g3)
    c: Distance(g0,g2) = 10
    c: Distance(g1,g3) = 4
    c: Coincident(g4,g5)
    c: Coincident(g5,g6)
    c: Coincident(g6,g7)
    c: Coincident(g7,g4)
    c: Horizontal(g4)
    c: Horizontal(g6)
    c: Vertical(g5)
    c: Vertical(g7)
    c: Distance(g5,g7) = 10
    c: Distance(g4,g6) = 4
    c: DistanceX(g0,g-3) = 2
    c: DistanceY(g-3,g0) = 1.5
    c: DistanceY(g4,g0) = 46
    c: DistanceX(g0,g4) = 0
FEATURE [PartDesign::Pad] Pad044  label="XLimitSwitchWireManagementRight"
  BaseFeature = -> LinearPattern001
  Direction = (0,-1,2e-16)
  Length = 5.8
  Length2 = 10
  Placement = pos=(0,0,0) rot=(1,0,0;1.5708rad)
  Profile = -> Sketch071
  ReferenceAxis = -> Sketch071 [N_Axis]
  Refine = true
  Suppressed = false
  Type = 0
FEATURE [PartDesign::Mirrored] Mirrored003  label="XLimitSwitchWireManagementLeft"
  BaseFeature = -> Pad044
  MirrorPlane = -> Sketch071 [V_Axis]
  Originals = -> [Pad044]
  Placement = pos=(0,0,0) rot=(1,0,0;1.5708rad)
  Refine = true
  Suppressed = false
  TransformMode = 0
FEATURE [Sketcher::SketchObject] Sketch073
  ArcFitTolerance = 1e-06
  AttachmentSupport = -> [Mirrored003]
  ExternalGeometry = -> [Mirrored003]
  FullyConstrained = false
  MakeInternals = false
  MapMode = 5
  Placement = pos=(0,1.04e-14,23.7) rot=(0,0,1;3.14159rad)
  sketch-geometry (5):
    g0: Circle CenterX=-25 CenterY=11.9 CenterZ=0 NormalX=0 NormalY=0 NormalZ=1 AngleXU=0 Radius=2
    g1: GeomPoint [constr] X=-25 Y=11.4714 Z=0
    g2: GeomPoint [constr] X=-20 Y=11.9 Z=0
    g3: GeomPoint [constr] X=-54.611 Y=11.9652 Z=0
    g4: GeomPoint X=-25 Y=14.8 Z=0
  constraints (6):
    c: Diameter(g0) = 4
    c: Symmetric(g-3,g-3,g2)
    c: DistanceX(g0,g1) = 0
    c: DistanceY(g2,g0) = 0
    c: Symmetric(g-4,g-4,g4)
    c: DistanceX(g0,g4) = 0
FEATURE [PartDesign::Pocket] Pocket029  label="XLimitSwitchWireManagementRightHole"
  BaseFeature = -> Mirrored003
  Direction = (0,0,-1)
  Length = 100
  Length2 = 5
  Placement = pos=(0,0,0) rot=(1,0,0;1.5708rad)
  Profile = -> Sketch073
  ReferenceAxis = -> Sketch073 [N_Axis]
  Refine = true
  Suppressed = false
  Type = 0
FEATURE [PartDesign::Mirrored] Mirrored004  label="XLimitSwitchWireManagementLeftHole"
  BaseFeature = -> Pocket029
  MirrorPlane = -> YZ_Plane
  Originals = -> [Pocket029]
  Placement = pos=(0,0,0) rot=(1,0,0;1.5708rad)
  Refine = true
  Suppressed = false
  TransformMode = 0
FEATURE [Sketcher::SketchObject] Sketch074
  ArcFitTolerance = 1e-06
  AttachmentSupport = -> [Mirrored004]
  FullyConstrained = true
  MakeInternals = false
  MapMode = 5
  Placement = pos=(0,-1.41e-14,-32) rot=(1,0,0;3.14159rad)
  sketch-geometry (4):
    g0: LineSegment StartX=5.5 StartY=0 StartZ=0 EndX=5.5 EndY=6 EndZ=0
    g1: LineSegment StartX=5.5 StartY=6 StartZ=0 EndX=-5.5 EndY=6 EndZ=0
    g2: LineSegment StartX=-5.5 StartY=6 StartZ=0 EndX=-5.5 EndY=0 EndZ=0
    g3: LineSegment StartX=-5.5 StartY=0 StartZ=0 EndX=5.5 EndY=0 EndZ=0
  constraints (11):
    c: Coincident(g0,g1)
    c: Coincident(g1,g2)
    c: Coincident(g2,g3)
    c: Coincident(g3,g0)
    c: Vertical(g0)
    c: Vertical(g2)
    c: Horizontal(g1)
    c: Horizontal(g3)
    c: Distance(g0,g2) = 11
    c: Distance(g1,g3) = 6
    c: Symmetric(g0,g2,g-1)
FEATURE [PartDesign::Pad] Pad045  label="MainWireManagement"
  BaseFeature = -> Mirrored004
  Direction = (0,0,-1)
  Length = 50
  Length2 = 10
  Placement = pos=(0,0,0) rot=(1,0,0;1.5708rad)
  Profile = -> Sketch074
  ReferenceAxis = -> Sketch074 [N_Axis]
  Refine = true
  Suppressed = false
  Type = 0
FEATURE [Sketcher::SketchObject] Sketch075
  ArcFitTolerance = 1e-06
  AttachmentSupport = -> [Pad045]
  ExternalGeometry = -> [Pad045]
  FullyConstrained = true
  MakeInternals = false
  MapMode = 5
  Placement = pos=(5.5,0,0) rot=(0.707107,0,0.707107;3.14159rad)
  sketch-geometry (8):
    g0: LineSegment StartX=-80 StartY=4 StartZ=0 EndX=-80 EndY=2 EndZ=0
    g1: LineSegment StartX=-80 StartY=2 StartZ=0 EndX=-69 EndY=2 EndZ=0
    g2: LineSegment StartX=-69 StartY=2 StartZ=0 EndX=-69 EndY=4 EndZ=0
    g3: LineSegment StartX=-69 StartY=4 StartZ=0 EndX=-80 EndY=4 EndZ=0
    g4: LineSegment StartX=-51 StartY=4 StartZ=0 EndX=-51 EndY=2 EndZ=0
    g5: LineSegment StartX=-51 StartY=2 StartZ=0 EndX=-40 EndY=2 EndZ=0
    g6: LineSegment StartX=-40 StartY=2 StartZ=0 EndX=-40 EndY=4 EndZ=0
    g7: LineSegment StartX=-40 StartY=4 StartZ=0 EndX=-51 EndY=4 EndZ=0
  constraints (24):
    c: Coincident(g0,g1)
    c: Coincident(g1,g2)
    c: Coincident(g2,g3)
    c: Coincident(g3,g0)
    c: Vertical(g0)
    c: Vertical(g2)
    c: Horizontal(g1)
    c: Horizontal(g3)
    c: Distance(g0,g2) = 11
    c: Distance(g1,g3) = 2
    c: DistanceY(g0,g-3) = 2
    c: DistanceX(g-3,g0) = 2
    c: Coincident(g4,g5)
    c: Coincident(g5,g6)
    c: Coincident(g6,g7)
    c: Coincident(g7,g4)
    c: Vertical(g4)
    c: Vertical(g6)
    c: Horizontal(g5)
    c: Horizontal(g7)
    c: Distance(g4,g6) = 11
    c: Distance(g5,g7) = 2
    c: DistanceY(g4,g2) = 0
    c: DistanceX(g2,g4) = 18
FEATURE [PartDesign::Pocket] Pocket030  label="MainWireManagementSlot"
  BaseFeature = -> Pad045
  Direction = (-1,0,2e-16)
  Length = 12
  Length2 = 5
  Placement = pos=(0,0,0) rot=(1,0,0;1.5708rad)
  Profile = -> Sketch075
  ReferenceAxis = -> Sketch075 [N_Axis]
  Refine = true
  Suppressed = false
  Type = 0
FEATURE [Sketcher::SketchObject] Sketch076
  ArcFitTolerance = 1e-06
  AttachmentSupport = -> [Pocket030]
  FullyConstrained = true
  MakeInternals = false
  MapMode = 5
  Placement = pos=(0,-9,2.8e-15) rot=(1,0,0;1.5708rad)
  sketch-geometry (2):
    g0: Circle CenterX=29 CenterY=-12.3 CenterZ=0 NormalX=0 NormalY=0 NormalZ=1 AngleXU=0 Radius=1.55
    g1: Circle CenterX=29 CenterY=-20.3 CenterZ=0 NormalX=0 NormalY=0 NormalZ=1 AngleXU=0 Radius=1.55
  constraints (6):
    c: Diameter(g0) = 3.1
    c: Diameter(g1) = 3.1
    c: DistanceY(g1,g0) = 8
    c: DistanceX(g0,g1) = 0
    c: DistanceX(g1,g-3) = 3
    c: DistanceY(g-3,g1) = 6
FEATURE [PartDesign::Pocket] Pocket031  label="ZLimitSwitchMountHoles"
  BaseFeature = -> Pocket030
  Direction = (0,1,-2e-16)
  Length = 10
  Length2 = 5
  Placement = pos=(0,0,0) rot=(1,0,0;1.5708rad)
  Profile = -> Sketch076
  ReferenceAxis = -> Sketch076 [N_Axis]
  Refine = true
  Suppressed = false
  Type = 0
FEATURE [Sketcher::SketchObject] Sketch077
  ArcFitTolerance = 1e-06
  AttachmentSupport = -> [YZ_Plane012]
  FullyConstrained = true
  MakeInternals = false
  MapMode = 5
  Placement = pos=(0,0,0) rot=(0.57735,0.57735,0.57735;2.0944rad)
  sketch-geometry (9):
    g0: LineSegment StartX=-16 StartY=-9.8 StartZ=0 EndX=4 EndY=-9.8 EndZ=0
    g1: LineSegment StartX=4 StartY=-9.8 StartZ=0 EndX=4 EndY=10 EndZ=0
    g2: LineSegment StartX=4 StartY=10 StartZ=0 EndX=-16 EndY=10 EndZ=0
    g3: LineSegment StartX=-16 StartY=10 StartZ=0 EndX=-16 EndY=-9.8 EndZ=0
    g4: GeomPoint [constr] X=0 Y=0 Z=0
    g5: LineSegment [constr] StartX=0 StartY=0 StartZ=0 EndX=4 EndY=0 EndZ=0
    g6: LineSegment [constr] StartX=4 StartY=0 StartZ=0 EndX=4 EndY=10 EndZ=0
    g7: LineSegment [constr] StartX=4 StartY=10 StartZ=0 EndX=0 EndY=10 EndZ=0
    g8: LineSegment [constr] StartX=0 StartY=10 StartZ=0 EndX=0 EndY=0 EndZ=0
  constraints (23):
    c: Coincident(g0,g1)
    c: Coincident(g1,g2)
    c: Coincident(g2,g3)
    c: Coincident(g3,g0)
    c: Horizontal(g0)
    c: Horizontal(g2)
    c: Vertical(g1)
    c: Vertical(g3)
    c: Distance(g1,g3) = 20
    c: Distance(g0,g2) = 19.8
    c: Coincident(g4,g-1)
    c: Coincident(g5,g6)
    c: Coincident(g6,g7)
    c: Coincident(g7,g8)
    c: Coincident(g8,g5)
    c: Horizontal(g5)
    c: Horizontal(g7)
    c: Vertical(g6)
    c: Vertical(g8)
    c: Coincident(g5,g4)
    c: Coincident(g6,g1)
    c: DistanceY(g8,g8) = 10
    c: DistanceX(g5,g5) = 4
FEATURE [PartDesign::Pad] Pad046  label="Base003"
  Direction = (1,0,0)
  Length = 6
  Length2 = 10
  Placement = pos=(0,0,0) rot=(1,1,1;2.0944rad)
  Profile = -> Sketch077
  ReferenceAxis = -> Sketch077 [N_Axis]
  Refine = true
  Suppressed = false
  Type = 0
FEATURE [Sketcher::SketchObject] Sketch078
  ArcFitTolerance = 1e-06
  AttachmentSupport = -> [Pad046]
  ExternalGeometry = -> [Pad046]
  FullyConstrained = true
  MakeInternals = false
  MapMode = 5
  Placement = pos=(-3.5e-15,-16,0) rot=(0.57735,0.57735,-0.57735;2.0944rad)
  sketch-geometry (2):
    g0: Circle CenterX=3.8 CenterY=3 CenterZ=0 NormalX=0 NormalY=0 NormalZ=1 AngleXU=0 Radius=1.6
    g1: Circle CenterX=-4.2 CenterY=3 CenterZ=0 NormalX=0 NormalY=0 NormalZ=1 AngleXU=0 Radius=1.6
  constraints (6):
    c: Diameter(g0) = 3.2
    c: Diameter(g1) = 3.2
    c: DistanceY(g0,g1) = 0
    c: DistanceX(g1,g0) = 8
    c: DistanceX(g0,g-3) = 6
    c: DistanceY(g0,g-3) = 3
FEATURE [PartDesign::Pocket] Pocket032  label="SwitchHolderMountHoles"
  BaseFeature = -> Pad046
  Direction = (0,1,0)
  Length = 40
  Length2 = 5
  Placement = pos=(0,0,0) rot=(1,1,1;2.0944rad)
  Profile = -> Sketch078
  ReferenceAxis = -> Sketch078 [N_Axis]
  Refine = true
  Suppressed = false
  Type = 0
FEATURE [Sketcher::SketchObject] Sketch079
  ArcFitTolerance = 1e-06
  AttachmentSupport = -> [Pocket032]
  ExternalGeometry = -> [Pocket032]
  FullyConstrained = true
  MakeInternals = false
  MapMode = 5
  Placement = pos=(0,0,0) rot=(0.57735,0.57735,-0.57735;4.18879rad)
  sketch-geometry (4):
    g0: LineSegment StartX=-16 StartY=-10 StartZ=0 EndX=0.8 EndY=-10 EndZ=0
    g1: LineSegment StartX=0.8 StartY=-10 StartZ=0 EndX=0.8 EndY=9.8 EndZ=0
    g2: LineSegment StartX=0.8 StartY=9.8 StartZ=0 EndX=-16 EndY=9.8 EndZ=0
    g3: LineSegment StartX=-16 StartY=9.8 StartZ=0 EndX=-16 EndY=-10 EndZ=0
  constraints (11):
    c: Coincident(g0,g1)
    c: Coincident(g1,g2)
    c: Coincident(g2,g3)
    c: Coincident(g3,g0)
    c: Horizontal(g0)
    c: Horizontal(g2)
    c: Vertical(g1)
    c: Vertical(g3)
    c: Distance(g1,g3) = 16.8
    c: Coincident(g0,g-4)
    c: DistanceY(g-5,g2) = 0
FEATURE [PartDesign::Pad] Pad047  label="SwitchPlatform"
  BaseFeature = -> Pocket032
  Direction = (-1,0,0)
  Length = 4
  Length2 = 10
  Placement = pos=(0,0,0) rot=(1,1,1;2.0944rad)
  Profile = -> Sketch079
  ReferenceAxis = -> Sketch079 [N_Axis]
  Refine = true
  Suppressed = false
  Type = 0
FEATURE [Sketcher::SketchObject] Sketch080
  ArcFitTolerance = 1e-06
  AttachmentSupport = -> [Pad047]
  ExternalGeometry = -> [Pad047]
  FullyConstrained = true
  MakeInternals = false
  MapMode = 5
  Placement = pos=(-4,0,0) rot=(0.57735,0.57735,-0.57735;4.18879rad)
  sketch-geometry (8):
    g0: LineSegment StartX=-16 StartY=-10 StartZ=0 EndX=-16 EndY=-2 EndZ=0
    g1: LineSegment StartX=-16 StartY=-2 StartZ=0 EndX=0.8 EndY=-2 EndZ=0
    g2: LineSegment StartX=0.8 StartY=-2 StartZ=0 EndX=0.8 EndY=-10 EndZ=0
    g3: LineSegment StartX=0.8 StartY=-10 StartZ=0 EndX=-1.2 EndY=-10 EndZ=0
    g4: LineSegment StartX=-1.2 StartY=-10 StartZ=0 EndX=-1.2 EndY=-4 EndZ=0
    g5: LineSegment StartX=-1.2 StartY=-4 StartZ=0 EndX=-14 EndY=-4 EndZ=0
    g6: LineSegment StartX=-14 StartY=-4 StartZ=0 EndX=-14 EndY=-10 EndZ=0
    g7: LineSegment StartX=-14 StartY=-10 StartZ=0 EndX=-16 EndY=-10 EndZ=0
  constraints (22):
    c: Coincident(g-4,g0)
    c: PointOnObject(g0,g-4)
    c: Coincident(g0,g1)
    c: Horizontal(g1)
    c: Coincident(g1,g2)
    c: Coincident(g2,g-3)
    c: Vertical(g2)
    c: Coincident(g2,g3)
    c: PointOnObject(g3,g-3)
    c: Coincident(g3,g4)
    c: Vertical(g4)
    c: Coincident(g4,g5)
    c: Horizontal(g5)
    c: Coincident(g5,g6)
    c: PointOnObject(g6,g-3)
    c: Vertical(g6)
    c: Coincident(g6,g7)
    c: Coincident(g7,g0)
    c: Equal(g7,g3)
    c: DistanceX(g3,g3) = 2
    c: DistanceY(g4,g4) = 6
    c: DistanceY(g5,g0) = 2
FEATURE [PartDesign::Pad] Pad048  label="SwitchCove"
  BaseFeature = -> Pad047
  Direction = (-1,0,0)
  Length = 5.8
  Length2 = 10
  Placement = pos=(0,0,0) rot=(1,1,1;2.0944rad)
  Profile = -> Sketch080
  ReferenceAxis = -> Sketch080 [N_Axis]
  Refine = true
  Suppressed = false
  Type = 0
FEATURE [Sketcher::SketchObject] Sketch081
  ArcFitTolerance = 1e-06
  AttachmentSupport = -> [Pad048]
  ExternalGeometry = -> [Pad048]
  FullyConstrained = true
  MakeInternals = false
  MapMode = 5
  Placement = pos=(0,9e-16,4) rot=(0,0,-1;1.5708rad)
  sketch-geometry (2):
    g0: GeomPoint [constr] X=1.2 Y=-4 Z=0
    g1: Circle CenterX=1.2 CenterY=-6.9 CenterZ=0 NormalX=0 NormalY=0 NormalZ=1 AngleXU=0 Radius=2
  constraints (3):
    c: Symmetric(g-5,g-5,g0)
    c: Diameter(g1) = 4
    c: Symmetric(g-4,g0,g1)
FEATURE [PartDesign::Pocket] Pocket033  label="SwitchPinHole"
  BaseFeature = -> Pad048
  Direction = (0,0,-1)
  Length = 5
  Length2 = 5
  Placement = pos=(0,0,0) rot=(1,1,1;2.0944rad)
  Profile = -> Sketch081
  ReferenceAxis = -> Sketch081 [N_Axis]
  Refine = true
  Suppressed = false
  Type = 0
FEATURE [PartDesign::LinearPattern] LinearPattern002  label="SwitchPinHoles"
  BaseFeature = -> Pocket033
  Direction = -> Sketch081 [H_Axis]
  Length = 12.8
  Mode = 0
  Occurrences = 3
  Offset = 6.4
  Originals = -> [Pocket033]
  Placement = pos=(0,0,0) rot=(1,1,1;2.0944rad)
  Refine = true
  Suppressed = false
  TransformMode = 0
FEATURE [Sketcher::SketchObject] Sketch082
  ArcFitTolerance = 1e-06
  AttachmentSupport = -> [LinearPattern002]
  ExternalGeometry = -> [LinearPattern002]
  FullyConstrained = true
  MakeInternals = false
  MapMode = 5
  Placement = pos=(-1.18e-14,-16,3.8e-15) rot=(0.57735,0.57735,-0.57735;2.0944rad)
  sketch-geometry (4):
    g0: LineSegment StartX=9.8 StartY=6 StartZ=0 EndX=-10 EndY=6 EndZ=0
    g1: LineSegment StartX=-10 StartY=6 StartZ=0 EndX=-10 EndY=1.95e-14 EndZ=0
    g2: LineSegment StartX=-10 StartY=1.94e-14 StartZ=0 EndX=9.8 EndY=1.94e-14 EndZ=0
    g3: LineSegment StartX=9.8 StartY=1.94e-14 StartZ=0 EndX=9.8 EndY=6 EndZ=0
  constraints (10):
    c: Coincident(g0,g1)
    c: Coincident(g1,g2)
    c: Coincident(g2,g3)
    c: Coincident(g3,g0)
    c: Horizontal(g2)
    c: Vertical(g1)
    c: Vertical(g3)
    c: Coincident(g0,g-6)
    c: Coincident(g0,g-5)
    c: DistanceY(g2,g-4) = 3
FEATURE [PartDesign::Pocket] Pocket034  label="MountHoleCutout"
  BaseFeature = -> LinearPattern002
  Direction = (0,1,0)
  Length = 10
  Length2 = 5
  Placement = pos=(0,0,0) rot=(1,1,1;2.0944rad)
  Profile = -> Sketch082
  ReferenceAxis = -> Sketch082 [N_Axis]
  Refine = true
  Suppressed = false
  Type = 0
FEATURE [PartDesign::Body] Body012  label="ZLimitSwitchHolder"
  AllowCompound = false
  Group = -> [Sketch077,Pad046,Sketch078,Pocket032,Sketch079,Pad047,Sketch080,Pad048,Sketch081,Pocket033,LinearPattern002,Sketch082,Pocket034]
  Origin = -> Origin012
  Placement = pos=(26,-13,-16.3) rot=(0,0,1;0rad)
  Tip = -> Pocket034
FEATURE [Sketcher::SketchObject] Sketch083
  ArcFitTolerance = 1e-06
  AttachmentSupport = -> [Pocket031]
  ExternalGeometry = -> [Pocket031]
  FullyConstrained = true
  MakeInternals = false
  MapMode = 5
  Placement = pos=(0,-9,2.8e-15) rot=(1,0,0;1.5708rad)
  sketch-geometry (1):
    g0: Circle CenterX=1.4 CenterY=-17.5 CenterZ=0 NormalX=0 NormalY=0 NormalZ=1 AngleXU=0 Radius=3.25
  constraints (2):
    c: Diameter(g0) = 6.5
    c: Coincident(g0,g-3)
FEATURE [PartDesign::Pocket] Pocket035  label="PlateMountHoleInset"
  BaseFeature = -> Pocket031
  Direction = (0,1,-2e-16)
  Length = 3.5
  Length2 = 5
  Placement = pos=(0,0,0) rot=(1,0,0;1.5708rad)
  Profile = -> Sketch083
  ReferenceAxis = -> Sketch083 [N_Axis]
  Refine = true
  Suppressed = false
  Type = 0
FEATURE [PartDesign::Body] Body  label="PlotterHeadv2"
  AllowCompound = false
  Group = -> [Sketch022,Pad020,Sketch023,Pocket003,Sketch024,Pocket004,Sketch025,Pocket005,Sketch026,Pocket006,Sketch030,Pocket009,Sketch031,Pad022,Sketch032,Pocket010,Sketch066,Pad040,Pad041,Mirrored,Pad042,Sketch067,Pad043,Mirrored001,Sketch068,Pocket027,LinearPattern,Sketch069,Pocket028,LinearPattern001,Sketch071,Pad044,Mirrored003,Sketch073,Pocket029,Mirrored004,Sketch074,Pad045,Sketch075,Pocket030,+4 more]
  Origin = -> Origin
  Tip = -> Pocket035
FEATURE [Sketcher::SketchObject] Sketch084
  ArcFitTolerance = 1e-06
  AttachmentSupport = -> [Pad024]
  ExternalGeometry = -> [Pad024]
  FullyConstrained = true
  MakeInternals = false
  MapMode = 5
  Placement = pos=(0,3e-16,0) rot=(-1,0,0;1.5708rad)
  sketch-geometry (4):
    g0: LineSegment StartX=21 StartY=16 StartZ=0 EndX=17 EndY=16 EndZ=0
    g1: LineSegment StartX=17 StartY=16 StartZ=0 EndX=17 EndY=10 EndZ=0
    g2: LineSegment StartX=17 StartY=10 StartZ=0 EndX=21 EndY=10 EndZ=0
    g3: LineSegment StartX=21 StartY=10 StartZ=0 EndX=21 EndY=16 EndZ=0
  constraints (12):
    c: Coincident(g0,g1)
    c: Coincident(g1,g2)
    c: Coincident(g2,g3)
    c: Coincident(g3,g0)
    c: Horizontal(g0)
    c: Horizontal(g2)
    c: Vertical(g1)
    c: Vertical(g3)
    c: Distance(g1,g3) = 4
    c: Distance(g0,g2) = 6
    c: DistanceY(g0,g-4) = 0
    c: DistanceX(g0,g-4) = 6
FEATURE [PartDesign::Pad] Pad049  label="ZLimitSwitchTrigger"
  BaseFeature = -> Pocket019
  Direction = (0,1,2e-16)
  Length = 14
  Length2 = 10
  Placement = pos=(0,0,0) rot=(1,0,0;1.5708rad)
  Profile = -> Sketch084
  ReferenceAxis = -> Sketch084 [N_Axis]
  Refine = true
  Suppressed = false
  Type = 0
FEATURE [Sketcher::SketchObject] Sketch085
  ArcFitTolerance = 1e-06
  AttachmentSupport = -> [Pad049]
  ExternalGeometry = -> [Pad049]
  FullyConstrained = true
  MakeInternals = false
  MapMode = 5
  Placement = pos=(0,3e-16,0) rot=(-1,0,0;1.5708rad)
  sketch-geometry (6):
    g0: LineSegment [constr] StartX=21 StartY=0 StartZ=0 EndX=-21 EndY=7 EndZ=0
    g1: LineSegment [constr] StartX=-21 StartY=7 StartZ=0 EndX=-21 EndY=-7 EndZ=0
    g2: LineSegment [constr] StartX=-21 StartY=-7 StartZ=0 EndX=21 EndY=0 EndZ=0
    g3: Circle CenterX=21 CenterY=0 CenterZ=0 NormalX=0 NormalY=0 NormalZ=1 AngleXU=0 Radius=3.975
    g4: Circle CenterX=-21 CenterY=7 CenterZ=0 NormalX=0 NormalY=0 NormalZ=1 AngleXU=0 Radius=3.975
    g5: Circle CenterX=-21 CenterY=-7 CenterZ=0 NormalX=0 NormalY=0 NormalZ=1 AngleXU=0 Radius=3.975
  constraints (14):
    c: PointOnObject(g0,g-1)
    c: Coincident(g0,g1)
    c: Coincident(g1,g2)
    c: Coincident(g2,g0)
    c: Symmetric(g0,g1,g-1)
    c: Coincident(g3,g0)
    c: Coincident(g5,g1)
    c: Equal(g5,g4)
    c: Equal(g4,g3)
    c: Diameter(g3) = 7.95
    c: Coincident(g4,g0)
    c: DistanceY(g1,g0) = 14
    c: DistanceX(g-6,g0) = 11
    c: DistanceX(g0,g-5) = 11
FEATURE [PartDesign::Pocket] Pocket036  label="ToolHolderMagnetInset"
  BaseFeature = -> Pad049
  Direction = (0,-1,-2e-16)
  Length = 5.2
  Length2 = 5
  Placement = pos=(0,0,0) rot=(1,0,0;1.5708rad)
  Profile = -> Sketch085
  ReferenceAxis = -> Sketch085 [N_Axis]
  Refine = true
  Suppressed = false
  Type = 0
FEATURE [PartDesign::Body] Body005  label="ToolMount"
  AllowCompound = false
  Group = -> [Sketch033,Pad023,Sketch034,Pad024,Sketch035,Pocket011,Sketch045,Pad030,Sketch046,Pocket016,Sketch047,Pocket017,Sketch048,Pocket018,Sketch049,Pocket019,Sketch084,Pad049,Sketch085,Pocket036]
  Origin = -> Origin005
  Placement = pos=(-1,-37,39.4) rot=(0,0,1;0rad)
  Tip = -> Pocket036
FEATURE [PartDesign::Mirrored] Mirrored005
  BaseFeature = -> Pocket024
  MirrorPlane = -> YZ_Plane010
  Originals = -> [Pad038]
  Placement = pos=(0,0,0) rot=(1,0,0;1.5708rad)
  Refine = true
  Suppressed = false
  TransformMode = 0
FEATURE [Sketcher::SketchObject] Sketch086
  ArcFitTolerance = 1e-06
  AttachmentSupport = -> [Mirrored005]
  ExternalGeometry = -> [Mirrored005]
  FullyConstrained = true
  MakeInternals = false
  MapMode = 5
  Placement = pos=(2.4e-15,-10,0) rot=(1,0,0;1.5708rad)
  sketch-geometry (3):
    g0: Circle CenterX=21 CenterY=0 CenterZ=0 NormalX=0 NormalY=0 NormalZ=1 AngleXU=0 Radius=3.975
    g1: Circle CenterX=-21 CenterY=7 CenterZ=0 NormalX=0 NormalY=0 NormalZ=1 AngleXU=0 Radius=3.975
    g2: Circle CenterX=-21 CenterY=-7 CenterZ=0 NormalX=0 NormalY=0 NormalZ=1 AngleXU=0 Radius=3.975
  constraints (8):
    c: PointOnObject(g0,g-1)
    c: Equal(g0,g1)
    c: Equal(g1,g2)
    c: Symmetric(g2,g1,g-1)
    c: DistanceY(g2,g1) = 14
    c: DistanceX(g-4,g0) = 11
    c: DistanceX(g1,g-3) = 11
    c: Diameter(g0) = 7.95
FEATURE [PartDesign::Pocket] Pocket037  label="ToolHolderMagnetInset001"
  BaseFeature = -> Mirrored005
  Direction = (0,1,-2e-16)
  Length = 7
  Length2 = 5
  Placement = pos=(0,0,0) rot=(1,0,0;1.5708rad)
  Profile = -> Sketch086
  ReferenceAxis = -> Sketch086 [N_Axis]
  Refine = true
  Suppressed = false
  Type = 0
FEATURE [PartDesign::Body] Body010  label="PenTool"
  AllowCompound = false
  Group = -> [Sketch056,Pad037,Sketch057,Pocket020,Sketch059,Pocket022,Sketch060,Pad038,Sketch062,Pocket024,Mirrored005,Sketch086,Pocket037]
  Origin = -> Origin010
  Placement = pos=(-1,-43.5,39.5) rot=(0,0,1;0rad)
  Tip = -> Pocket037
